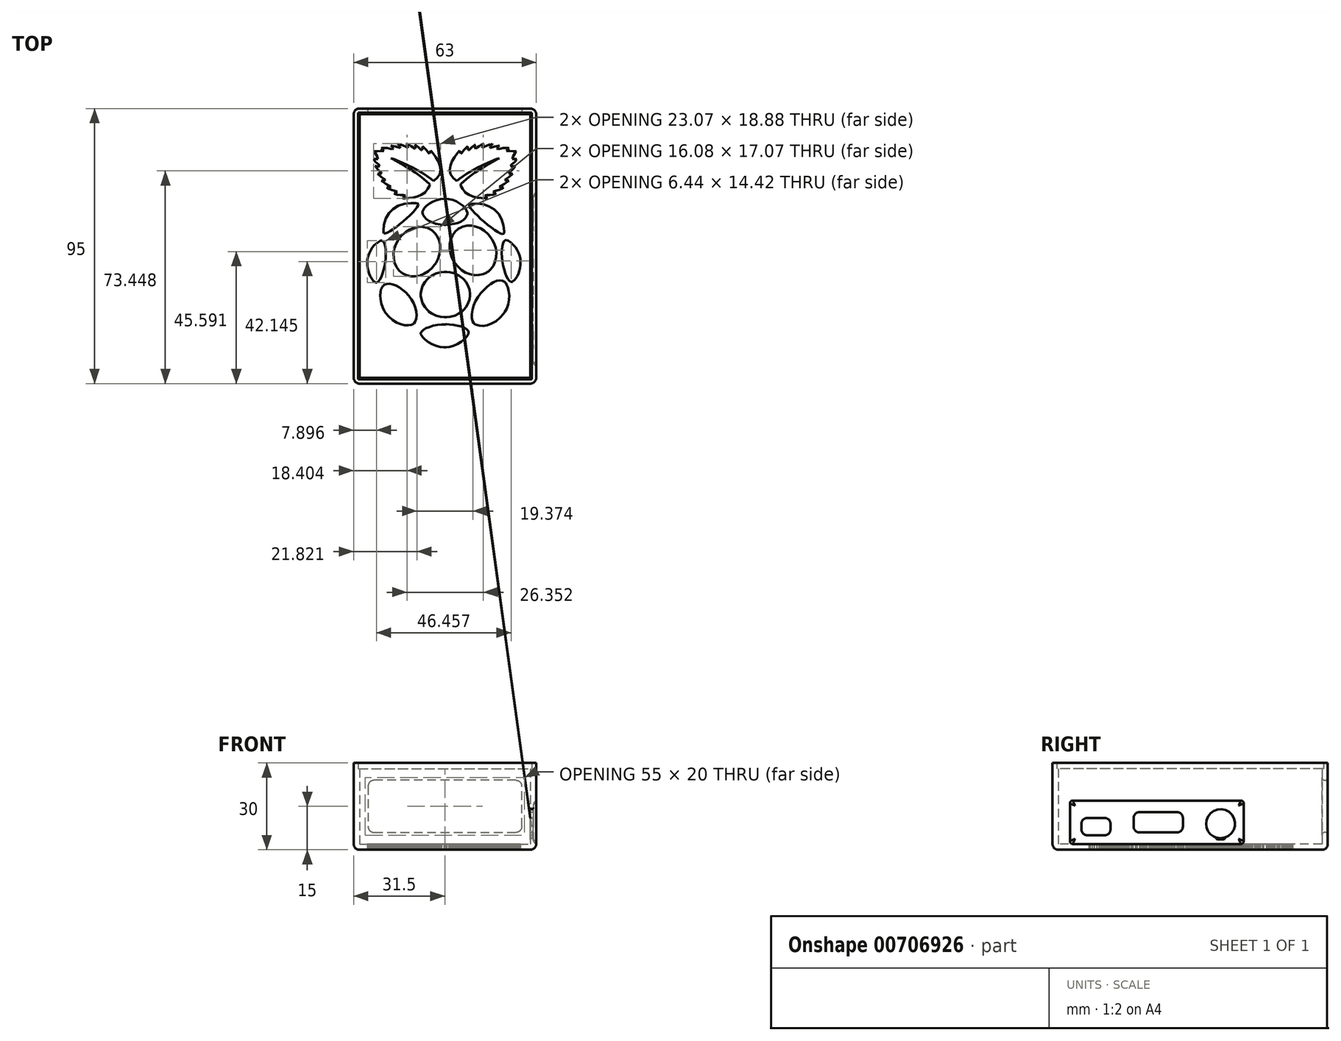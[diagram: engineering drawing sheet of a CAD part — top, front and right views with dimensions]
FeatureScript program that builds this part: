
annotation { "Feature Type Name" : "Feature", "Feature Type Description" : "" }
export const myFeature = defineFeature(function(context is Context, id is Id, definition is map)
    precondition{}
    {
        {
            var Q0;
            Q0=qCreatedBy(makeId("Top.planeOp"),FACE);
            var sketch = newSketch(context, id + "F0", { "sketchPlane" : qUnion([Q0])});
            skLineSegment(sketch, "E0.bottom", {"start": v(-30, 46) * mm, "end": v(30, 46) * mm});
            skLineSegment(sketch, "E0.top", {"start": v(-30, -46) * mm, "end": v(30, -46) * mm});
            skLineSegment(sketch, "E0.left", {"start": v(-30, 46) * mm, "end": v(-30, -46) * mm});
            skLineSegment(sketch, "E0.right", {"start": v(30, 46) * mm, "end": v(30, -46) * mm});
            skLineSegment(sketch, "E1.bottom", {"start": v(-29.5, 45.5) * mm, "end": v(29.5, 45.5) * mm});
            skLineSegment(sketch, "E1.top", {"start": v(-29.5, -45.5) * mm, "end": v(29.5, -45.5) * mm});
            skLineSegment(sketch, "E1.left", {"start": v(-29.5, 45.5) * mm, "end": v(-29.5, -45.5) * mm});
            skLineSegment(sketch, "E1.right", {"start": v(29.5, 45.5) * mm, "end": v(29.5, -45.5) * mm});
            skLineSegment(sketch, "E2.bottom", {"start": v(-31.5, 47.5) * mm, "end": v(31.5, 47.5) * mm});
            skLineSegment(sketch, "E2.top", {"start": v(-31.5, -47.5) * mm, "end": v(31.5, -47.5) * mm});
            skLineSegment(sketch, "E2.left", {"start": v(-31.5, 47.5) * mm, "end": v(-31.5, -47.5) * mm});
            skLineSegment(sketch, "E2.right", {"start": v(31.5, 47.5) * mm, "end": v(31.5, -47.5) * mm});
            skPoint(sketch, "E3", {"position": v(-30, 0) * mm});
            skPoint(sketch, "E4", {"position": v(0, 46) * mm});
            skLineSegment(sketch, "E5", {"start": v(-13.39, 37.27) * mm, "end": v(-13.48, 37.27) * mm});
            skLineSegment(sketch, "E6", {"start": v(-13.48, 37.27) * mm, "end": v(-13.98, 37.15) * mm});
            skLineSegment(sketch, "E7", {"start": v(-13.98, 37.15) * mm, "end": v(-14.52, 36.85) * mm});
            skLineSegment(sketch, "E8", {"start": v(-14.52, 36.85) * mm, "end": v(-14.63, 36.76) * mm});
            skLineSegment(sketch, "E9", {"start": v(-14.63, 36.76) * mm, "end": v(-14.83, 36.84) * mm});
            skLineSegment(sketch, "E10", {"start": v(-14.83, 36.84) * mm, "end": v(-15.47, 37.02) * mm});
            skLineSegment(sketch, "E11", {"start": v(-15.47, 37.02) * mm, "end": v(-16.29, 37.1) * mm});
            skLineSegment(sketch, "E12", {"start": v(-16.29, 37.1) * mm, "end": v(-17.08, 36.94) * mm});
            skLineSegment(sketch, "E13", {"start": v(-17.08, 36.94) * mm, "end": v(-17.67, 36.6) * mm});
            skLineSegment(sketch, "E14", {"start": v(-17.67, 36.6) * mm, "end": v(-17.83, 36.46) * mm});
            skLineSegment(sketch, "E15", {"start": v(-17.83, 36.46) * mm, "end": v(-18.07, 36.5) * mm});
            skLineSegment(sketch, "E16", {"start": v(-18.07, 36.5) * mm, "end": v(-18.79, 36.5) * mm});
            skLineSegment(sketch, "E17", {"start": v(-18.79, 36.5) * mm, "end": v(-19.44, 36.37) * mm});
            skLineSegment(sketch, "E18", {"start": v(-19.44, 36.37) * mm, "end": v(-19.89, 36.11) * mm});
            skLineSegment(sketch, "E19", {"start": v(-19.89, 36.11) * mm, "end": v(-20.13, 35.87) * mm});
            skLineSegment(sketch, "E20", {"start": v(-20.13, 35.87) * mm, "end": v(-20.2, 35.78) * mm});
            skLineSegment(sketch, "E21", {"start": v(-20.2, 35.78) * mm, "end": v(-20.25, 35.78) * mm});
            skLineSegment(sketch, "E22", {"start": v(-20.25, 35.78) * mm, "end": v(-20.4, 35.8) * mm});
            skLineSegment(sketch, "E23", {"start": v(-20.4, 35.8) * mm, "end": v(-20.75, 35.81) * mm});
            skLineSegment(sketch, "E24", {"start": v(-20.75, 35.81) * mm, "end": v(-21.19, 35.81) * mm});
            skLineSegment(sketch, "E25", {"start": v(-21.19, 35.81) * mm, "end": v(-21.7, 35.77) * mm});
            skLineSegment(sketch, "E26", {"start": v(-21.7, 35.77) * mm, "end": v(-22.23, 35.66) * mm});
            skLineSegment(sketch, "E27", {"start": v(-22.23, 35.66) * mm, "end": v(-22.76, 35.45) * mm});
            skLineSegment(sketch, "E28", {"start": v(-22.76, 35.45) * mm, "end": v(-23.25, 35.12) * mm});
            skLineSegment(sketch, "E29", {"start": v(-23.25, 35.12) * mm, "end": v(-23.58, 34.78) * mm});
            skLineSegment(sketch, "E30", {"start": v(-23.58, 34.78) * mm, "end": v(-23.67, 34.65) * mm});
            skLineSegment(sketch, "E31", {"start": v(-23.67, 34.65) * mm, "end": v(-23.88, 34.68) * mm});
            skLineSegment(sketch, "E32", {"start": v(-23.88, 34.68) * mm, "end": v(-24.52, 34.67) * mm});
            skLineSegment(sketch, "E33", {"start": v(-24.52, 34.67) * mm, "end": v(-25.21, 34.52) * mm});
            skLineSegment(sketch, "E34", {"start": v(-25.21, 34.52) * mm, "end": v(-25.74, 34.23) * mm});
            skLineSegment(sketch, "E35", {"start": v(-25.74, 34.23) * mm, "end": v(-26.12, 33.83) * mm});
            skLineSegment(sketch, "E36", {"start": v(-26.12, 33.83) * mm, "end": v(-26.34, 33.33) * mm});
            skLineSegment(sketch, "E37", {"start": v(-26.34, 33.33) * mm, "end": v(-26.4, 32.77) * mm});
            skLineSegment(sketch, "E38", {"start": v(-26.4, 32.77) * mm, "end": v(-26.3, 32.18) * mm});
            skLineSegment(sketch, "E39", {"start": v(-26.3, 32.18) * mm, "end": v(-26.12, 31.7) * mm});
            skLineSegment(sketch, "E40", {"start": v(-26.12, 31.7) * mm, "end": v(-26.04, 31.56) * mm});
            skLineSegment(sketch, "E41", {"start": v(-26.04, 31.56) * mm, "end": v(-26.14, 31.42) * mm});
            skLineSegment(sketch, "E42", {"start": v(-26.14, 31.42) * mm, "end": v(-26.4, 30.96) * mm});
            skLineSegment(sketch, "E43", {"start": v(-26.4, 30.96) * mm, "end": v(-26.6, 30.3) * mm});
            skLineSegment(sketch, "E44", {"start": v(-26.6, 30.3) * mm, "end": v(-26.48, 29.5) * mm});
            skLineSegment(sketch, "E45", {"start": v(-26.48, 29.5) * mm, "end": v(-26.07, 28.74) * mm});
            skLineSegment(sketch, "E46", {"start": v(-26.07, 28.74) * mm, "end": v(-25.9, 28.51) * mm});
            skLineSegment(sketch, "E47", {"start": v(-25.9, 28.51) * mm, "end": v(-25.96, 28.37) * mm});
            skLineSegment(sketch, "E48", {"start": v(-25.96, 28.37) * mm, "end": v(-26.08, 27.87) * mm});
            skLineSegment(sketch, "E49", {"start": v(-26.08, 27.87) * mm, "end": v(-26, 27.2) * mm});
            skLineSegment(sketch, "E50", {"start": v(-26, 27.2) * mm, "end": v(-25.67, 26.47) * mm});
            skLineSegment(sketch, "E51", {"start": v(-25.67, 26.47) * mm, "end": v(-25.23, 25.87) * mm});
            skLineSegment(sketch, "E52", {"start": v(-25.23, 25.87) * mm, "end": v(-25.06, 25.69) * mm});
            skLineSegment(sketch, "E53", {"start": v(-25.06, 25.69) * mm, "end": v(-25.1, 25.49) * mm});
            skLineSegment(sketch, "E54", {"start": v(-25.1, 25.49) * mm, "end": v(-25.12, 24.87) * mm});
            skLineSegment(sketch, "E55", {"start": v(-25.12, 24.87) * mm, "end": v(-24.92, 24.17) * mm});
            skLineSegment(sketch, "E56", {"start": v(-24.92, 24.17) * mm, "end": v(-24.5, 23.57) * mm});
            skLineSegment(sketch, "E57", {"start": v(-24.5, 23.57) * mm, "end": v(-24.06, 23.16) * mm});
            skLineSegment(sketch, "E58", {"start": v(-24.06, 23.16) * mm, "end": v(-23.9, 23.05) * mm});
            skLineSegment(sketch, "E59", {"start": v(-23.9, 23.05) * mm, "end": v(-23.92, 22.79) * mm});
            skLineSegment(sketch, "E60", {"start": v(-23.92, 22.79) * mm, "end": v(-23.73, 21.97) * mm});
            skLineSegment(sketch, "E61", {"start": v(-23.73, 21.97) * mm, "end": v(-23.16, 21.14) * mm});
            skLineSegment(sketch, "E62", {"start": v(-23.16, 21.14) * mm, "end": v(-22.47, 20.55) * mm});
            skLineSegment(sketch, "E63", {"start": v(-22.47, 20.55) * mm, "end": v(-22.06, 20.27) * mm});
            skLineSegment(sketch, "E64", {"start": v(-22.06, 20.27) * mm, "end": v(-21.94, 20.19) * mm});
            skLineSegment(sketch, "E65", {"start": v(-21.94, 20.19) * mm, "end": v(-21.9, 20.01) * mm});
            skLineSegment(sketch, "E66", {"start": v(-21.9, 20.01) * mm, "end": v(-21.74, 19.5) * mm});
            skLineSegment(sketch, "E67", {"start": v(-21.74, 19.5) * mm, "end": v(-21.34, 18.87) * mm});
            skLineSegment(sketch, "E68", {"start": v(-21.34, 18.87) * mm, "end": v(-20.63, 18.32) * mm});
            skLineSegment(sketch, "E69", {"start": v(-20.63, 18.32) * mm, "end": v(-19.78, 17.97) * mm});
            skLineSegment(sketch, "E70", {"start": v(-19.78, 17.97) * mm, "end": v(-19.49, 17.89) * mm});
            skLineSegment(sketch, "E71", {"start": v(-19.49, 17.89) * mm, "end": v(-19.44, 17.67) * mm});
            skLineSegment(sketch, "E72", {"start": v(-19.44, 17.67) * mm, "end": v(-19.12, 17.04) * mm});
            skLineSegment(sketch, "E73", {"start": v(-19.12, 17.04) * mm, "end": v(-18.52, 16.52) * mm});
            skLineSegment(sketch, "E74", {"start": v(-18.52, 16.52) * mm, "end": v(-17.78, 16.2) * mm});
            skLineSegment(sketch, "E75", {"start": v(-17.78, 16.2) * mm, "end": v(-17.17, 16.02) * mm});
            skLineSegment(sketch, "E76", {"start": v(-17.17, 16.02) * mm, "end": v(-16.96, 15.97) * mm});
            skLineSegment(sketch, "E77", {"start": v(-16.96, 15.97) * mm, "end": v(-17.3, 15.77) * mm});
            skLineSegment(sketch, "E78", {"start": v(-17.3, 15.77) * mm, "end": v(-18.29, 15.15) * mm});
            skLineSegment(sketch, "E79", {"start": v(-18.29, 15.15) * mm, "end": v(-19.53, 14.22) * mm});
            skLineSegment(sketch, "E80", {"start": v(-19.53, 14.22) * mm, "end": v(-20.66, 13.16) * mm});
            skLineSegment(sketch, "E81", {"start": v(-20.66, 13.16) * mm, "end": v(-21.66, 11.92) * mm});
            skLineSegment(sketch, "E82", {"start": v(-21.66, 11.92) * mm, "end": v(-22.48, 10.46) * mm});
            skLineSegment(sketch, "E83", {"start": v(-22.48, 10.46) * mm, "end": v(-23.1, 8.74) * mm});
            skLineSegment(sketch, "E84", {"start": v(-23.1, 8.74) * mm, "end": v(-23.5, 6.72) * mm});
            skLineSegment(sketch, "E85", {"start": v(-23.5, 6.72) * mm, "end": v(-23.63, 4.96) * mm});
            skLineSegment(sketch, "E86", {"start": v(-23.63, 4.96) * mm, "end": v(-23.63, 4.37) * mm});
            skLineSegment(sketch, "E87", {"start": v(-23.63, 4.37) * mm, "end": v(-24.16, 3.43) * mm});
            skLineSegment(sketch, "E88", {"start": v(-24.16, 3.43) * mm, "end": v(-24.36, 3.3) * mm});
            skLineSegment(sketch, "E89", {"start": v(-24.36, 3.3) * mm, "end": v(-24.93, 2.9) * mm});
            skLineSegment(sketch, "E90", {"start": v(-24.93, 2.9) * mm, "end": v(-25.67, 2.24) * mm});
            skLineSegment(sketch, "E91", {"start": v(-25.67, 2.24) * mm, "end": v(-26.38, 1.47) * mm});
            skLineSegment(sketch, "E92", {"start": v(-26.38, 1.47) * mm, "end": v(-27.04, 0.61) * mm});
            skLineSegment(sketch, "E93", {"start": v(-27.04, 0.61) * mm, "end": v(-27.63, -0.34) * mm});
            skLineSegment(sketch, "E94", {"start": v(-27.63, -0.34) * mm, "end": v(-28.15, -1.37) * mm});
            skLineSegment(sketch, "E95", {"start": v(-28.15, -1.37) * mm, "end": v(-28.58, -2.47) * mm});
            skLineSegment(sketch, "E96", {"start": v(-28.58, -2.47) * mm, "end": v(-28.9, -3.62) * mm});
            skLineSegment(sketch, "E97", {"start": v(-28.9, -3.62) * mm, "end": v(-29.11, -4.83) * mm});
            skLineSegment(sketch, "E98", {"start": v(-29.11, -4.83) * mm, "end": v(-29.2, -6.07) * mm});
            skLineSegment(sketch, "E99", {"start": v(-29.2, -6.07) * mm, "end": v(-29.13, -7.34) * mm});
            skLineSegment(sketch, "E100", {"start": v(-29.13, -7.34) * mm, "end": v(-28.9, -8.62) * mm});
            skLineSegment(sketch, "E101", {"start": v(-28.9, -8.62) * mm, "end": v(-28.52, -9.9) * mm});
            skLineSegment(sketch, "E102", {"start": v(-28.52, -9.9) * mm, "end": v(-27.94, -11.2) * mm});
            skLineSegment(sketch, "E103", {"start": v(-27.94, -11.2) * mm, "end": v(-27.17, -12.47) * mm});
            skLineSegment(sketch, "E104", {"start": v(-27.17, -12.47) * mm, "end": v(-26.46, -13.42) * mm});
            skLineSegment(sketch, "E105", {"start": v(-26.46, -13.42) * mm, "end": v(-26.2, -13.71) * mm});
            skLineSegment(sketch, "E106", {"start": v(-26.2, -13.71) * mm, "end": v(-26.13, -14.07) * mm});
            skLineSegment(sketch, "E107", {"start": v(-26.13, -14.07) * mm, "end": v(-25.87, -15.15) * mm});
            skLineSegment(sketch, "E108", {"start": v(-25.87, -15.15) * mm, "end": v(-25.47, -16.45) * mm});
            skLineSegment(sketch, "E109", {"start": v(-25.47, -16.45) * mm, "end": v(-25.04, -17.66) * mm});
            skLineSegment(sketch, "E110", {"start": v(-25.04, -17.66) * mm, "end": v(-24.72, -18.57) * mm});
            skLineSegment(sketch, "E111", {"start": v(-24.72, -18.57) * mm, "end": v(-24.61, -18.87) * mm});
            skLineSegment(sketch, "E112", {"start": v(-24.61, -18.87) * mm, "end": v(-24.54, -19.45) * mm});
            skLineSegment(sketch, "E113", {"start": v(-24.54, -19.45) * mm, "end": v(-24.1, -21.17) * mm});
            skLineSegment(sketch, "E114", {"start": v(-24.1, -21.17) * mm, "end": v(-23.23, -23.16) * mm});
            skLineSegment(sketch, "E115", {"start": v(-23.23, -23.16) * mm, "end": v(-22.14, -24.84) * mm});
            skLineSegment(sketch, "E116", {"start": v(-22.14, -24.84) * mm, "end": v(-20.92, -26.2) * mm});
            skLineSegment(sketch, "E117", {"start": v(-20.92, -26.2) * mm, "end": v(-19.67, -27.3) * mm});
            skLineSegment(sketch, "E118", {"start": v(-19.67, -27.3) * mm, "end": v(-18.5, -28.1) * mm});
            skLineSegment(sketch, "E119", {"start": v(-18.5, -28.1) * mm, "end": v(-17.5, -28.62) * mm});
            skLineSegment(sketch, "E120", {"start": v(-17.5, -28.62) * mm, "end": v(-16.96, -28.84) * mm});
            skLineSegment(sketch, "E121", {"start": v(-16.96, -28.84) * mm, "end": v(-16.78, -28.9) * mm});
            skLineSegment(sketch, "E122", {"start": v(-16.78, -28.9) * mm, "end": v(-16.37, -29.2) * mm});
            skLineSegment(sketch, "E123", {"start": v(-16.37, -29.2) * mm, "end": v(-15.14, -30.09) * mm});
            skLineSegment(sketch, "E124", {"start": v(-15.14, -30.09) * mm, "end": v(-13.38, -31.22) * mm});
            skLineSegment(sketch, "E125", {"start": v(-13.38, -31.22) * mm, "end": v(-11.45, -32.25) * mm});
            skLineSegment(sketch, "E126", {"start": v(-11.45, -32.25) * mm, "end": v(-9.83, -32.95) * mm});
            skLineSegment(sketch, "E127", {"start": v(-9.83, -32.95) * mm, "end": v(-9.28, -33.15) * mm});
            skLineSegment(sketch, "E128", {"start": v(-9.28, -33.15) * mm, "end": v(-8.77, -33.67) * mm});
            skLineSegment(sketch, "E129", {"start": v(-8.77, -33.67) * mm, "end": v(-7.06, -35.05) * mm});
            skLineSegment(sketch, "E130", {"start": v(-7.06, -35.05) * mm, "end": v(-4.77, -36.34) * mm});
            skLineSegment(sketch, "E131", {"start": v(-4.77, -36.34) * mm, "end": v(-2.44, -37.05) * mm});
            skLineSegment(sketch, "E132", {"start": v(-2.44, -37.05) * mm, "end": v(-0.66, -37.28) * mm});
            skLineSegment(sketch, "E133", {"start": v(-0.66, -37.28) * mm, "end": v(-0.07, -37.28) * mm});
            skLineSegment(sketch, "E134", {"start": v(-0.07, -37.28) * mm, "end": v(-0.04, -37.28) * mm});
            skLineSegment(sketch, "E135", {"start": v(-0.04, -37.28) * mm, "end": v(0.06, -37.28) * mm});
            skLineSegment(sketch, "E136", {"start": v(0.06, -37.28) * mm, "end": v(0.07, -37.28) * mm});
            skLineSegment(sketch, "E137", {"start": v(0.07, -37.28) * mm, "end": v(0.66, -37.28) * mm});
            skLineSegment(sketch, "E138", {"start": v(0.66, -37.28) * mm, "end": v(2.44, -37.06) * mm});
            skLineSegment(sketch, "E139", {"start": v(2.44, -37.06) * mm, "end": v(4.77, -36.34) * mm});
            skLineSegment(sketch, "E140", {"start": v(4.77, -36.34) * mm, "end": v(7.06, -35.05) * mm});
            skLineSegment(sketch, "E141", {"start": v(7.06, -35.05) * mm, "end": v(8.77, -33.67) * mm});
            skLineSegment(sketch, "E142", {"start": v(8.77, -33.67) * mm, "end": v(9.28, -33.15) * mm});
            skLineSegment(sketch, "E143", {"start": v(9.28, -33.15) * mm, "end": v(9.83, -32.95) * mm});
            skLineSegment(sketch, "E144", {"start": v(9.83, -32.95) * mm, "end": v(11.45, -32.25) * mm});
            skLineSegment(sketch, "E145", {"start": v(11.45, -32.25) * mm, "end": v(13.38, -31.22) * mm});
            skLineSegment(sketch, "E146", {"start": v(13.38, -31.22) * mm, "end": v(15.14, -30.09) * mm});
            skLineSegment(sketch, "E147", {"start": v(15.14, -30.09) * mm, "end": v(16.37, -29.2) * mm});
            skLineSegment(sketch, "E148", {"start": v(16.37, -29.2) * mm, "end": v(16.78, -28.9) * mm});
            skLineSegment(sketch, "E149", {"start": v(16.78, -28.9) * mm, "end": v(16.96, -28.84) * mm});
            skLineSegment(sketch, "E150", {"start": v(16.96, -28.84) * mm, "end": v(17.5, -28.62) * mm});
            skLineSegment(sketch, "E151", {"start": v(17.5, -28.62) * mm, "end": v(18.5, -28.1) * mm});
            skLineSegment(sketch, "E152", {"start": v(18.5, -28.1) * mm, "end": v(19.67, -27.3) * mm});
            skLineSegment(sketch, "E153", {"start": v(19.67, -27.3) * mm, "end": v(20.92, -26.2) * mm});
            skLineSegment(sketch, "E154", {"start": v(20.92, -26.2) * mm, "end": v(22.14, -24.84) * mm});
            skLineSegment(sketch, "E155", {"start": v(22.14, -24.84) * mm, "end": v(23.23, -23.16) * mm});
            skLineSegment(sketch, "E156", {"start": v(23.23, -23.16) * mm, "end": v(24.1, -21.17) * mm});
            skLineSegment(sketch, "E157", {"start": v(24.1, -21.17) * mm, "end": v(24.54, -19.45) * mm});
            skLineSegment(sketch, "E158", {"start": v(24.54, -19.45) * mm, "end": v(24.61, -18.87) * mm});
            skLineSegment(sketch, "E159", {"start": v(24.61, -18.87) * mm, "end": v(24.72, -18.57) * mm});
            skLineSegment(sketch, "E160", {"start": v(24.72, -18.57) * mm, "end": v(25.04, -17.66) * mm});
            skLineSegment(sketch, "E161", {"start": v(25.04, -17.66) * mm, "end": v(25.47, -16.45) * mm});
            skLineSegment(sketch, "E162", {"start": v(25.47, -16.45) * mm, "end": v(25.87, -15.15) * mm});
            skLineSegment(sketch, "E163", {"start": v(25.87, -15.15) * mm, "end": v(26.13, -14.07) * mm});
            skLineSegment(sketch, "E164", {"start": v(26.13, -14.07) * mm, "end": v(26.2, -13.71) * mm});
            skLineSegment(sketch, "E165", {"start": v(26.2, -13.71) * mm, "end": v(26.46, -13.42) * mm});
            skLineSegment(sketch, "E166", {"start": v(26.46, -13.42) * mm, "end": v(27.17, -12.47) * mm});
            skLineSegment(sketch, "E167", {"start": v(27.17, -12.47) * mm, "end": v(27.94, -11.2) * mm});
            skLineSegment(sketch, "E168", {"start": v(27.94, -11.2) * mm, "end": v(28.52, -9.9) * mm});
            skLineSegment(sketch, "E169", {"start": v(28.52, -9.9) * mm, "end": v(28.9, -8.62) * mm});
            skLineSegment(sketch, "E170", {"start": v(28.9, -8.62) * mm, "end": v(29.13, -7.34) * mm});
            skLineSegment(sketch, "E171", {"start": v(29.13, -7.34) * mm, "end": v(29.2, -6.07) * mm});
            skLineSegment(sketch, "E172", {"start": v(29.2, -6.07) * mm, "end": v(29.11, -4.83) * mm});
            skLineSegment(sketch, "E173", {"start": v(29.11, -4.83) * mm, "end": v(28.9, -3.62) * mm});
            skLineSegment(sketch, "E174", {"start": v(28.9, -3.62) * mm, "end": v(28.58, -2.47) * mm});
            skLineSegment(sketch, "E175", {"start": v(28.58, -2.47) * mm, "end": v(28.15, -1.37) * mm});
            skLineSegment(sketch, "E176", {"start": v(28.15, -1.37) * mm, "end": v(27.63, -0.34) * mm});
            skLineSegment(sketch, "E177", {"start": v(27.63, -0.34) * mm, "end": v(27.03, 0.61) * mm});
            skLineSegment(sketch, "E178", {"start": v(27.03, 0.61) * mm, "end": v(26.38, 1.48) * mm});
            skLineSegment(sketch, "E179", {"start": v(26.38, 1.48) * mm, "end": v(25.67, 2.24) * mm});
            skLineSegment(sketch, "E180", {"start": v(25.67, 2.24) * mm, "end": v(24.93, 2.9) * mm});
            skLineSegment(sketch, "E181", {"start": v(24.93, 2.9) * mm, "end": v(24.36, 3.3) * mm});
            skLineSegment(sketch, "E182", {"start": v(24.36, 3.3) * mm, "end": v(24.16, 3.43) * mm});
            skLineSegment(sketch, "E183", {"start": v(24.16, 3.43) * mm, "end": v(23.63, 4.37) * mm});
            skLineSegment(sketch, "E184", {"start": v(23.63, 4.37) * mm, "end": v(23.63, 4.96) * mm});
            skLineSegment(sketch, "E185", {"start": v(23.63, 4.96) * mm, "end": v(23.5, 6.72) * mm});
            skLineSegment(sketch, "E186", {"start": v(23.5, 6.72) * mm, "end": v(23.1, 8.74) * mm});
            skLineSegment(sketch, "E187", {"start": v(23.1, 8.74) * mm, "end": v(22.48, 10.46) * mm});
            skLineSegment(sketch, "E188", {"start": v(22.48, 10.46) * mm, "end": v(21.65, 11.92) * mm});
            skLineSegment(sketch, "E189", {"start": v(21.65, 11.92) * mm, "end": v(20.66, 13.16) * mm});
            skLineSegment(sketch, "E190", {"start": v(20.66, 13.16) * mm, "end": v(19.53, 14.22) * mm});
            skLineSegment(sketch, "E191", {"start": v(19.53, 14.22) * mm, "end": v(18.28, 15.15) * mm});
            skLineSegment(sketch, "E192", {"start": v(18.28, 15.15) * mm, "end": v(17.3, 15.77) * mm});
            skLineSegment(sketch, "E193", {"start": v(17.3, 15.77) * mm, "end": v(16.96, 15.97) * mm});
            skLineSegment(sketch, "E194", {"start": v(16.96, 15.97) * mm, "end": v(17.17, 16.02) * mm});
            skLineSegment(sketch, "E195", {"start": v(17.17, 16.02) * mm, "end": v(17.77, 16.2) * mm});
            skLineSegment(sketch, "E196", {"start": v(17.77, 16.2) * mm, "end": v(18.52, 16.52) * mm});
            skLineSegment(sketch, "E197", {"start": v(18.52, 16.52) * mm, "end": v(19.12, 17.05) * mm});
            skLineSegment(sketch, "E198", {"start": v(19.12, 17.05) * mm, "end": v(19.44, 17.67) * mm});
            skLineSegment(sketch, "E199", {"start": v(19.44, 17.67) * mm, "end": v(19.49, 17.9) * mm});
            skLineSegment(sketch, "E200", {"start": v(19.49, 17.9) * mm, "end": v(19.78, 17.97) * mm});
            skLineSegment(sketch, "E201", {"start": v(19.78, 17.97) * mm, "end": v(20.63, 18.32) * mm});
            skLineSegment(sketch, "E202", {"start": v(20.63, 18.32) * mm, "end": v(21.34, 18.87) * mm});
            skLineSegment(sketch, "E203", {"start": v(21.34, 18.87) * mm, "end": v(21.74, 19.5) * mm});
            skLineSegment(sketch, "E204", {"start": v(21.74, 19.5) * mm, "end": v(21.9, 20.02) * mm});
            skLineSegment(sketch, "E205", {"start": v(21.9, 20.02) * mm, "end": v(21.94, 20.19) * mm});
            skLineSegment(sketch, "E206", {"start": v(21.94, 20.19) * mm, "end": v(22.06, 20.27) * mm});
            skLineSegment(sketch, "E207", {"start": v(22.06, 20.27) * mm, "end": v(22.47, 20.55) * mm});
            skLineSegment(sketch, "E208", {"start": v(22.47, 20.55) * mm, "end": v(23.16, 21.14) * mm});
            skLineSegment(sketch, "E209", {"start": v(23.16, 21.14) * mm, "end": v(23.73, 21.97) * mm});
            skLineSegment(sketch, "E210", {"start": v(23.73, 21.97) * mm, "end": v(23.92, 22.79) * mm});
            skLineSegment(sketch, "E211", {"start": v(23.92, 22.79) * mm, "end": v(23.9, 23.05) * mm});
            skLineSegment(sketch, "E212", {"start": v(23.9, 23.05) * mm, "end": v(24.06, 23.16) * mm});
            skLineSegment(sketch, "E213", {"start": v(24.06, 23.16) * mm, "end": v(24.5, 23.57) * mm});
            skLineSegment(sketch, "E214", {"start": v(24.5, 23.57) * mm, "end": v(24.92, 24.17) * mm});
            skLineSegment(sketch, "E215", {"start": v(24.92, 24.17) * mm, "end": v(25.12, 24.87) * mm});
            skLineSegment(sketch, "E216", {"start": v(25.12, 24.87) * mm, "end": v(25.1, 25.5) * mm});
            skLineSegment(sketch, "E217", {"start": v(25.1, 25.5) * mm, "end": v(25.06, 25.69) * mm});
            skLineSegment(sketch, "E218", {"start": v(25.06, 25.69) * mm, "end": v(25.23, 25.87) * mm});
            skLineSegment(sketch, "E219", {"start": v(25.23, 25.87) * mm, "end": v(25.67, 26.47) * mm});
            skLineSegment(sketch, "E220", {"start": v(25.67, 26.47) * mm, "end": v(26, 27.2) * mm});
            skLineSegment(sketch, "E221", {"start": v(26, 27.2) * mm, "end": v(26.08, 27.87) * mm});
            skLineSegment(sketch, "E222", {"start": v(26.08, 27.87) * mm, "end": v(25.96, 28.37) * mm});
            skLineSegment(sketch, "E223", {"start": v(25.96, 28.37) * mm, "end": v(25.89, 28.51) * mm});
            skLineSegment(sketch, "E224", {"start": v(25.89, 28.51) * mm, "end": v(26.07, 28.74) * mm});
            skLineSegment(sketch, "E225", {"start": v(26.07, 28.74) * mm, "end": v(26.48, 29.5) * mm});
            skLineSegment(sketch, "E226", {"start": v(26.48, 29.5) * mm, "end": v(26.6, 30.3) * mm});
            skLineSegment(sketch, "E227", {"start": v(26.6, 30.3) * mm, "end": v(26.4, 30.97) * mm});
            skLineSegment(sketch, "E228", {"start": v(26.4, 30.97) * mm, "end": v(26.14, 31.42) * mm});
            skLineSegment(sketch, "E229", {"start": v(26.14, 31.42) * mm, "end": v(26.04, 31.56) * mm});
            skLineSegment(sketch, "E230", {"start": v(26.04, 31.56) * mm, "end": v(26.12, 31.7) * mm});
            skLineSegment(sketch, "E231", {"start": v(26.12, 31.7) * mm, "end": v(26.3, 32.18) * mm});
            skLineSegment(sketch, "E232", {"start": v(26.3, 32.18) * mm, "end": v(26.4, 32.77) * mm});
            skLineSegment(sketch, "E233", {"start": v(26.4, 32.77) * mm, "end": v(26.33, 33.33) * mm});
            skLineSegment(sketch, "E234", {"start": v(26.33, 33.33) * mm, "end": v(26.12, 33.83) * mm});
            skLineSegment(sketch, "E235", {"start": v(26.12, 33.83) * mm, "end": v(25.74, 34.23) * mm});
            skLineSegment(sketch, "E236", {"start": v(25.74, 34.23) * mm, "end": v(25.2, 34.52) * mm});
            skLineSegment(sketch, "E237", {"start": v(25.2, 34.52) * mm, "end": v(24.52, 34.67) * mm});
            skLineSegment(sketch, "E238", {"start": v(24.52, 34.67) * mm, "end": v(23.88, 34.68) * mm});
            skLineSegment(sketch, "E239", {"start": v(23.88, 34.68) * mm, "end": v(23.67, 34.65) * mm});
            skLineSegment(sketch, "E240", {"start": v(23.67, 34.65) * mm, "end": v(23.58, 34.78) * mm});
            skLineSegment(sketch, "E241", {"start": v(23.58, 34.78) * mm, "end": v(23.25, 35.12) * mm});
            skLineSegment(sketch, "E242", {"start": v(23.25, 35.12) * mm, "end": v(22.76, 35.45) * mm});
            skLineSegment(sketch, "E243", {"start": v(22.76, 35.45) * mm, "end": v(22.23, 35.66) * mm});
            skLineSegment(sketch, "E244", {"start": v(22.23, 35.66) * mm, "end": v(21.7, 35.77) * mm});
            skLineSegment(sketch, "E245", {"start": v(21.7, 35.77) * mm, "end": v(21.19, 35.81) * mm});
            skLineSegment(sketch, "E246", {"start": v(21.19, 35.81) * mm, "end": v(20.75, 35.81) * mm});
            skLineSegment(sketch, "E247", {"start": v(20.75, 35.81) * mm, "end": v(20.4, 35.8) * mm});
            skLineSegment(sketch, "E248", {"start": v(20.4, 35.8) * mm, "end": v(20.25, 35.78) * mm});
            skLineSegment(sketch, "E249", {"start": v(20.25, 35.78) * mm, "end": v(20.2, 35.78) * mm});
            skLineSegment(sketch, "E250", {"start": v(20.2, 35.78) * mm, "end": v(20.13, 35.87) * mm});
            skLineSegment(sketch, "E251", {"start": v(20.13, 35.87) * mm, "end": v(19.89, 36.11) * mm});
            skLineSegment(sketch, "E252", {"start": v(19.89, 36.11) * mm, "end": v(19.44, 36.37) * mm});
            skLineSegment(sketch, "E253", {"start": v(19.44, 36.37) * mm, "end": v(18.78, 36.5) * mm});
            skLineSegment(sketch, "E254", {"start": v(18.78, 36.5) * mm, "end": v(18.07, 36.5) * mm});
            skLineSegment(sketch, "E255", {"start": v(18.07, 36.5) * mm, "end": v(17.83, 36.46) * mm});
            skLineSegment(sketch, "E256", {"start": v(17.83, 36.46) * mm, "end": v(17.67, 36.6) * mm});
            skLineSegment(sketch, "E257", {"start": v(17.67, 36.6) * mm, "end": v(17.08, 36.94) * mm});
            skLineSegment(sketch, "E258", {"start": v(17.08, 36.94) * mm, "end": v(16.29, 37.1) * mm});
            skLineSegment(sketch, "E259", {"start": v(16.29, 37.1) * mm, "end": v(15.47, 37.02) * mm});
            skLineSegment(sketch, "E260", {"start": v(15.47, 37.02) * mm, "end": v(14.83, 36.84) * mm});
            skLineSegment(sketch, "E261", {"start": v(14.83, 36.84) * mm, "end": v(14.63, 36.76) * mm});
            skLineSegment(sketch, "E262", {"start": v(14.63, 36.76) * mm, "end": v(14.43, 36.92) * mm});
            skLineSegment(sketch, "E263", {"start": v(14.43, 36.92) * mm, "end": v(13.7, 37.23) * mm});
            skLineSegment(sketch, "E264", {"start": v(13.7, 37.23) * mm, "end": v(12.89, 37.22) * mm});
            skLineSegment(sketch, "E265", {"start": v(12.89, 37.22) * mm, "end": v(12.14, 36.95) * mm});
            skLineSegment(sketch, "E266", {"start": v(12.14, 36.95) * mm, "end": v(11.58, 36.71) * mm});
            skLineSegment(sketch, "E267", {"start": v(11.58, 36.71) * mm, "end": v(11.4, 36.65) * mm});
            skLineSegment(sketch, "E268", {"start": v(11.4, 36.65) * mm, "end": v(11.15, 36.73) * mm});
            skLineSegment(sketch, "E269", {"start": v(11.15, 36.73) * mm, "end": v(10.38, 36.84) * mm});
            skLineSegment(sketch, "E270", {"start": v(10.38, 36.84) * mm, "end": v(9.69, 36.71) * mm});
            skLineSegment(sketch, "E271", {"start": v(9.69, 36.71) * mm, "end": v(9.15, 36.43) * mm});
            skLineSegment(sketch, "E272", {"start": v(9.15, 36.43) * mm, "end": v(8.74, 36.21) * mm});
            skLineSegment(sketch, "E273", {"start": v(8.74, 36.21) * mm, "end": v(8.6, 36.16) * mm});
            skLineSegment(sketch, "E274", {"start": v(8.6, 36.16) * mm, "end": v(8.33, 36.22) * mm});
            skLineSegment(sketch, "E275", {"start": v(8.33, 36.22) * mm, "end": v(7.48, 36.23) * mm});
            skLineSegment(sketch, "E276", {"start": v(7.48, 36.23) * mm, "end": v(6.68, 35.97) * mm});
            skLineSegment(sketch, "E277", {"start": v(6.68, 35.97) * mm, "end": v(6.05, 35.48) * mm});
            skLineSegment(sketch, "E278", {"start": v(6.05, 35.48) * mm, "end": v(5.6, 35.01) * mm});
            skLineSegment(sketch, "E279", {"start": v(5.6, 35.01) * mm, "end": v(5.45, 34.86) * mm});
            skLineSegment(sketch, "E280", {"start": v(5.45, 34.86) * mm, "end": v(4.46, 34.88) * mm});
            skLineSegment(sketch, "E281", {"start": v(4.46, 34.88) * mm, "end": v(4.21, 34.73) * mm});
            skLineSegment(sketch, "E282", {"start": v(4.21, 34.73) * mm, "end": v(3.52, 34.22) * mm});
            skLineSegment(sketch, "E283", {"start": v(3.52, 34.22) * mm, "end": v(2.7, 33.44) * mm});
            skLineSegment(sketch, "E284", {"start": v(2.7, 33.44) * mm, "end": v(2, 32.6) * mm});
            skLineSegment(sketch, "E285", {"start": v(2, 32.6) * mm, "end": v(1.4, 31.7) * mm});
            skLineSegment(sketch, "E286", {"start": v(1.4, 31.7) * mm, "end": v(0.91, 30.8) * mm});
            skLineSegment(sketch, "E287", {"start": v(0.91, 30.8) * mm, "end": v(0.52, 29.94) * mm});
            skLineSegment(sketch, "E288", {"start": v(0.52, 29.94) * mm, "end": v(0.22, 29.14) * mm});
            skLineSegment(sketch, "E289", {"start": v(0.22, 29.14) * mm, "end": v(0.05, 28.63) * mm});
            skLineSegment(sketch, "E290", {"start": v(0.05, 28.63) * mm, "end": v(0, 28.46) * mm});
            skLineSegment(sketch, "E291", {"start": v(0, 28.46) * mm, "end": v(-0.05, 28.63) * mm});
            skLineSegment(sketch, "E292", {"start": v(-0.05, 28.63) * mm, "end": v(-0.22, 29.14) * mm});
            skLineSegment(sketch, "E293", {"start": v(-0.22, 29.14) * mm, "end": v(-0.52, 29.94) * mm});
            skLineSegment(sketch, "E294", {"start": v(-0.52, 29.94) * mm, "end": v(-0.92, 30.8) * mm});
            skLineSegment(sketch, "E295", {"start": v(-0.92, 30.8) * mm, "end": v(-1.4, 31.7) * mm});
            skLineSegment(sketch, "E296", {"start": v(-1.4, 31.7) * mm, "end": v(-2, 32.6) * mm});
            skLineSegment(sketch, "E297", {"start": v(-2, 32.6) * mm, "end": v(-2.7, 33.44) * mm});
            skLineSegment(sketch, "E298", {"start": v(-2.7, 33.44) * mm, "end": v(-3.52, 34.22) * mm});
            skLineSegment(sketch, "E299", {"start": v(-3.52, 34.22) * mm, "end": v(-4.22, 34.73) * mm});
            skLineSegment(sketch, "E300", {"start": v(-4.22, 34.73) * mm, "end": v(-4.46, 34.88) * mm});
            skLineSegment(sketch, "E301", {"start": v(-4.46, 34.88) * mm, "end": v(-5.45, 34.86) * mm});
            skLineSegment(sketch, "E302", {"start": v(-5.45, 34.86) * mm, "end": v(-5.6, 35.01) * mm});
            skLineSegment(sketch, "E303", {"start": v(-5.6, 35.01) * mm, "end": v(-6.05, 35.48) * mm});
            skLineSegment(sketch, "E304", {"start": v(-6.05, 35.48) * mm, "end": v(-6.68, 35.97) * mm});
            skLineSegment(sketch, "E305", {"start": v(-6.68, 35.97) * mm, "end": v(-7.48, 36.23) * mm});
            skLineSegment(sketch, "E306", {"start": v(-7.48, 36.23) * mm, "end": v(-8.33, 36.22) * mm});
            skLineSegment(sketch, "E307", {"start": v(-8.33, 36.22) * mm, "end": v(-8.6, 36.16) * mm});
            skLineSegment(sketch, "E308", {"start": v(-8.6, 36.16) * mm, "end": v(-8.75, 36.21) * mm});
            skLineSegment(sketch, "E309", {"start": v(-8.75, 36.21) * mm, "end": v(-9.15, 36.43) * mm});
            skLineSegment(sketch, "E310", {"start": v(-9.15, 36.43) * mm, "end": v(-9.69, 36.71) * mm});
            skLineSegment(sketch, "E311", {"start": v(-9.69, 36.71) * mm, "end": v(-10.38, 36.84) * mm});
            skLineSegment(sketch, "E312", {"start": v(-10.38, 36.84) * mm, "end": v(-11.15, 36.73) * mm});
            skLineSegment(sketch, "E313", {"start": v(-11.15, 36.73) * mm, "end": v(-11.4, 36.65) * mm});
            skLineSegment(sketch, "E314", {"start": v(-11.4, 36.65) * mm, "end": v(-11.52, 36.69) * mm});
            skLineSegment(sketch, "E315", {"start": v(-11.52, 36.69) * mm, "end": v(-11.88, 36.84) * mm});
            skLineSegment(sketch, "E316", {"start": v(-11.88, 36.84) * mm, "end": v(-12.37, 37.05) * mm});
            skLineSegment(sketch, "E317", {"start": v(-12.37, 37.05) * mm, "end": v(-12.87, 37.22) * mm});
            skLineSegment(sketch, "E318", {"start": v(-12.87, 37.22) * mm, "end": v(-13.26, 37.28) * mm});
            skLineSegment(sketch, "E319", {"start": v(-13.26, 37.28) * mm, "end": v(-13.39, 37.27) * mm});
            skLineSegment(sketch, "E320", {"start": v(-13.39, 37.27) * mm, "end": v(-13.39, 37.27) * mm});
            skLineSegment(sketch, "E321", {"start": v(-18.7, 30.36) * mm, "end": v(-18.07, 30.03) * mm});
            skLineSegment(sketch, "E322", {"start": v(-18.07, 30.03) * mm, "end": v(-16.18, 29.02) * mm});
            skLineSegment(sketch, "E323", {"start": v(-16.18, 29.02) * mm, "end": v(-13.93, 27.75) * mm});
            skLineSegment(sketch, "E324", {"start": v(-13.93, 27.75) * mm, "end": v(-11.93, 26.53) * mm});
            skLineSegment(sketch, "E325", {"start": v(-11.93, 26.53) * mm, "end": v(-10.17, 25.37) * mm});
            skLineSegment(sketch, "E326", {"start": v(-10.17, 25.37) * mm, "end": v(-8.63, 24.27) * mm});
            skLineSegment(sketch, "E327", {"start": v(-8.63, 24.27) * mm, "end": v(-7.3, 23.21) * mm});
            skLineSegment(sketch, "E328", {"start": v(-7.3, 23.21) * mm, "end": v(-6.19, 22.2) * mm});
            skLineSegment(sketch, "E329", {"start": v(-6.19, 22.2) * mm, "end": v(-5.48, 21.5) * mm});
            skLineSegment(sketch, "E330", {"start": v(-5.48, 21.5) * mm, "end": v(-5.25, 21.24) * mm});
            skLineSegment(sketch, "E331", {"start": v(-5.25, 21.24) * mm, "end": v(-5.35, 20.84) * mm});
            skLineSegment(sketch, "E332", {"start": v(-5.35, 20.84) * mm, "end": v(-5.9, 19.7) * mm});
            skLineSegment(sketch, "E333", {"start": v(-5.9, 19.7) * mm, "end": v(-6.9, 18.54) * mm});
            skLineSegment(sketch, "E334", {"start": v(-6.9, 18.54) * mm, "end": v(-8.15, 17.69) * mm});
            skLineSegment(sketch, "E335", {"start": v(-8.15, 17.69) * mm, "end": v(-9.55, 17.1) * mm});
            skLineSegment(sketch, "E336", {"start": v(-9.55, 17.1) * mm, "end": v(-11, 16.75) * mm});
            skLineSegment(sketch, "E337", {"start": v(-11, 16.75) * mm, "end": v(-12.4, 16.56) * mm});
            skLineSegment(sketch, "E338", {"start": v(-12.4, 16.56) * mm, "end": v(-13.64, 16.5) * mm});
            skLineSegment(sketch, "E339", {"start": v(-13.64, 16.5) * mm, "end": v(-14.38, 16.52) * mm});
            skLineSegment(sketch, "E340", {"start": v(-14.38, 16.52) * mm, "end": v(-14.63, 16.53) * mm});
            skLineSegment(sketch, "E341", {"start": v(-14.63, 16.53) * mm, "end": v(-14.55, 16.57) * mm});
            skLineSegment(sketch, "E342", {"start": v(-14.55, 16.57) * mm, "end": v(-14.3, 16.7) * mm});
            skLineSegment(sketch, "E343", {"start": v(-14.3, 16.7) * mm, "end": v(-14.03, 16.9) * mm});
            skLineSegment(sketch, "E344", {"start": v(-14.03, 16.9) * mm, "end": v(-13.81, 17.12) * mm});
            skLineSegment(sketch, "E345", {"start": v(-13.81, 17.12) * mm, "end": v(-13.7, 17.31) * mm});
            skLineSegment(sketch, "E346", {"start": v(-13.7, 17.31) * mm, "end": v(-13.67, 17.38) * mm});
            skLineSegment(sketch, "E347", {"start": v(-13.67, 17.38) * mm, "end": v(-13.8, 17.47) * mm});
            skLineSegment(sketch, "E348", {"start": v(-13.8, 17.47) * mm, "end": v(-14.32, 17.57) * mm});
            skLineSegment(sketch, "E349", {"start": v(-14.32, 17.57) * mm, "end": v(-15.3, 17.65) * mm});
            skLineSegment(sketch, "E350", {"start": v(-15.3, 17.65) * mm, "end": v(-16.44, 17.8) * mm});
            skLineSegment(sketch, "E351", {"start": v(-16.44, 17.8) * mm, "end": v(-17.3, 18.05) * mm});
            skLineSegment(sketch, "E352", {"start": v(-17.3, 18.05) * mm, "end": v(-17.55, 18.2) * mm});
            skLineSegment(sketch, "E353", {"start": v(-17.55, 18.2) * mm, "end": v(-17.46, 18.21) * mm});
            skLineSegment(sketch, "E354", {"start": v(-17.46, 18.21) * mm, "end": v(-17.2, 18.28) * mm});
            skLineSegment(sketch, "E355", {"start": v(-17.2, 18.28) * mm, "end": v(-16.94, 18.39) * mm});
            skLineSegment(sketch, "E356", {"start": v(-16.94, 18.39) * mm, "end": v(-16.72, 18.55) * mm});
            skLineSegment(sketch, "E357", {"start": v(-16.72, 18.55) * mm, "end": v(-16.57, 18.73) * mm});
            skLineSegment(sketch, "E358", {"start": v(-16.57, 18.73) * mm, "end": v(-16.53, 18.8) * mm});
            skLineSegment(sketch, "E359", {"start": v(-16.53, 18.8) * mm, "end": v(-16.78, 18.87) * mm});
            skLineSegment(sketch, "E360", {"start": v(-16.78, 18.87) * mm, "end": v(-17.51, 19.1) * mm});
            skLineSegment(sketch, "E361", {"start": v(-17.51, 19.1) * mm, "end": v(-18.46, 19.42) * mm});
            skLineSegment(sketch, "E362", {"start": v(-18.46, 19.42) * mm, "end": v(-19.32, 19.79) * mm});
            skLineSegment(sketch, "E363", {"start": v(-19.32, 19.79) * mm, "end": v(-19.87, 20.11) * mm});
            skLineSegment(sketch, "E364", {"start": v(-19.87, 20.11) * mm, "end": v(-20.03, 20.24) * mm});
            skLineSegment(sketch, "E365", {"start": v(-20.03, 20.24) * mm, "end": v(-19.95, 20.24) * mm});
            skLineSegment(sketch, "E366", {"start": v(-19.95, 20.24) * mm, "end": v(-19.7, 20.23) * mm});
            skLineSegment(sketch, "E367", {"start": v(-19.7, 20.23) * mm, "end": v(-19.37, 20.24) * mm});
            skLineSegment(sketch, "E368", {"start": v(-19.37, 20.24) * mm, "end": v(-19, 20.33) * mm});
            skLineSegment(sketch, "E369", {"start": v(-19, 20.33) * mm, "end": v(-18.7, 20.48) * mm});
            skLineSegment(sketch, "E370", {"start": v(-18.7, 20.48) * mm, "end": v(-18.6, 20.55) * mm});
            skLineSegment(sketch, "E371", {"start": v(-18.6, 20.55) * mm, "end": v(-18.9, 20.7) * mm});
            skLineSegment(sketch, "E372", {"start": v(-18.9, 20.7) * mm, "end": v(-20.35, 21.46) * mm});
            skLineSegment(sketch, "E373", {"start": v(-20.35, 21.46) * mm, "end": v(-21.72, 22.38) * mm});
            skLineSegment(sketch, "E374", {"start": v(-21.72, 22.38) * mm, "end": v(-21.96, 22.62) * mm});
            skLineSegment(sketch, "E375", {"start": v(-21.96, 22.62) * mm, "end": v(-21.84, 22.62) * mm});
            skLineSegment(sketch, "E376", {"start": v(-21.84, 22.62) * mm, "end": v(-21.5, 22.63) * mm});
            skLineSegment(sketch, "E377", {"start": v(-21.5, 22.63) * mm, "end": v(-21.09, 22.65) * mm});
            skLineSegment(sketch, "E378", {"start": v(-21.09, 22.65) * mm, "end": v(-20.74, 22.72) * mm});
            skLineSegment(sketch, "E379", {"start": v(-20.74, 22.72) * mm, "end": v(-20.56, 22.8) * mm});
            skLineSegment(sketch, "E380", {"start": v(-20.56, 22.8) * mm, "end": v(-20.52, 22.84) * mm});
            skLineSegment(sketch, "E381", {"start": v(-20.52, 22.84) * mm, "end": v(-20.8, 23) * mm});
            skLineSegment(sketch, "E382", {"start": v(-20.8, 23) * mm, "end": v(-22, 23.88) * mm});
            skLineSegment(sketch, "E383", {"start": v(-22, 23.88) * mm, "end": v(-23.03, 24.83) * mm});
            skLineSegment(sketch, "E384", {"start": v(-23.03, 24.83) * mm, "end": v(-23.22, 25.03) * mm});
            skLineSegment(sketch, "E385", {"start": v(-23.22, 25.03) * mm, "end": v(-23.08, 25.01) * mm});
            skLineSegment(sketch, "E386", {"start": v(-23.08, 25.01) * mm, "end": v(-22.68, 24.99) * mm});
            skLineSegment(sketch, "E387", {"start": v(-22.68, 24.99) * mm, "end": v(-22.28, 25) * mm});
            skLineSegment(sketch, "E388", {"start": v(-22.28, 25) * mm, "end": v(-22, 25.06) * mm});
            skLineSegment(sketch, "E389", {"start": v(-22, 25.06) * mm, "end": v(-21.87, 25.13) * mm});
            skLineSegment(sketch, "E390", {"start": v(-21.87, 25.13) * mm, "end": v(-21.82, 25.16) * mm});
            skLineSegment(sketch, "E391", {"start": v(-21.82, 25.16) * mm, "end": v(-21.98, 25.31) * mm});
            skLineSegment(sketch, "E392", {"start": v(-21.98, 25.31) * mm, "end": v(-22.45, 25.76) * mm});
            skLineSegment(sketch, "E393", {"start": v(-22.45, 25.76) * mm, "end": v(-23.1, 26.35) * mm});
            skLineSegment(sketch, "E394", {"start": v(-23.1, 26.35) * mm, "end": v(-23.67, 26.98) * mm});
            skLineSegment(sketch, "E395", {"start": v(-23.67, 26.98) * mm, "end": v(-24.03, 27.5) * mm});
            skLineSegment(sketch, "E396", {"start": v(-24.03, 27.5) * mm, "end": v(-24.12, 27.68) * mm});
            skLineSegment(sketch, "E397", {"start": v(-24.12, 27.68) * mm, "end": v(-24.01, 27.65) * mm});
            skLineSegment(sketch, "E398", {"start": v(-24.01, 27.65) * mm, "end": v(-23.67, 27.55) * mm});
            skLineSegment(sketch, "E399", {"start": v(-23.67, 27.55) * mm, "end": v(-23.24, 27.5) * mm});
            skLineSegment(sketch, "E400", {"start": v(-23.24, 27.5) * mm, "end": v(-22.86, 27.54) * mm});
            skLineSegment(sketch, "E401", {"start": v(-22.86, 27.54) * mm, "end": v(-22.6, 27.65) * mm});
            skLineSegment(sketch, "E402", {"start": v(-22.6, 27.65) * mm, "end": v(-22.52, 27.7) * mm});
            skLineSegment(sketch, "E403", {"start": v(-22.52, 27.7) * mm, "end": v(-22.58, 27.83) * mm});
            skLineSegment(sketch, "E404", {"start": v(-22.58, 27.83) * mm, "end": v(-22.87, 28.14) * mm});
            skLineSegment(sketch, "E405", {"start": v(-22.87, 28.14) * mm, "end": v(-23.43, 28.6) * mm});
            skLineSegment(sketch, "E406", {"start": v(-23.43, 28.6) * mm, "end": v(-24.06, 29.22) * mm});
            skLineSegment(sketch, "E407", {"start": v(-24.06, 29.22) * mm, "end": v(-24.52, 29.87) * mm});
            skLineSegment(sketch, "E408", {"start": v(-24.52, 29.87) * mm, "end": v(-24.63, 30.11) * mm});
            skLineSegment(sketch, "E409", {"start": v(-24.63, 30.11) * mm, "end": v(-24.5, 30.1) * mm});
            skLineSegment(sketch, "E410", {"start": v(-24.5, 30.1) * mm, "end": v(-24.14, 30.07) * mm});
            skLineSegment(sketch, "E411", {"start": v(-24.14, 30.07) * mm, "end": v(-23.7, 30.04) * mm});
            skLineSegment(sketch, "E412", {"start": v(-23.7, 30.04) * mm, "end": v(-23.34, 30.04) * mm});
            skLineSegment(sketch, "E413", {"start": v(-23.34, 30.04) * mm, "end": v(-23.18, 30.08) * mm});
            skLineSegment(sketch, "E414", {"start": v(-23.18, 30.08) * mm, "end": v(-23.14, 30.11) * mm});
            skLineSegment(sketch, "E415", {"start": v(-23.14, 30.11) * mm, "end": v(-23.2, 30.33) * mm});
            skLineSegment(sketch, "E416", {"start": v(-23.2, 30.33) * mm, "end": v(-23.4, 30.95) * mm});
            skLineSegment(sketch, "E417", {"start": v(-23.4, 30.95) * mm, "end": v(-23.73, 31.63) * mm});
            skLineSegment(sketch, "E418", {"start": v(-23.73, 31.63) * mm, "end": v(-24.1, 32.22) * mm});
            skLineSegment(sketch, "E419", {"start": v(-24.1, 32.22) * mm, "end": v(-24.38, 32.63) * mm});
            skLineSegment(sketch, "E420", {"start": v(-24.38, 32.63) * mm, "end": v(-24.48, 32.77) * mm});
            skLineSegment(sketch, "E421", {"start": v(-24.48, 32.77) * mm, "end": v(-24.2, 32.77) * mm});
            skLineSegment(sketch, "E422", {"start": v(-24.2, 32.77) * mm, "end": v(-23.34, 32.78) * mm});
            skLineSegment(sketch, "E423", {"start": v(-23.34, 32.78) * mm, "end": v(-22.2, 32.79) * mm});
            skLineSegment(sketch, "E424", {"start": v(-22.2, 32.79) * mm, "end": v(-21.35, 32.82) * mm});
            skLineSegment(sketch, "E425", {"start": v(-21.35, 32.82) * mm, "end": v(-21.05, 32.88) * mm});
            skLineSegment(sketch, "E426", {"start": v(-21.05, 32.88) * mm, "end": v(-21.92, 33.77) * mm});
            skLineSegment(sketch, "E427", {"start": v(-21.92, 33.77) * mm, "end": v(-21.67, 33.83) * mm});
            skLineSegment(sketch, "E428", {"start": v(-21.67, 33.83) * mm, "end": v(-20.9, 33.9) * mm});
            skLineSegment(sketch, "E429", {"start": v(-20.9, 33.9) * mm, "end": v(-19.9, 33.83) * mm});
            skLineSegment(sketch, "E430", {"start": v(-19.9, 33.83) * mm, "end": v(-18.96, 33.63) * mm});
            skLineSegment(sketch, "E431", {"start": v(-18.96, 33.63) * mm, "end": v(-18.34, 33.45) * mm});
            skLineSegment(sketch, "E432", {"start": v(-18.34, 33.45) * mm, "end": v(-18.13, 33.39) * mm});
            skLineSegment(sketch, "E433", {"start": v(-18.13, 33.39) * mm, "end": v(-18.07, 33.44) * mm});
            skLineSegment(sketch, "E434", {"start": v(-18.07, 33.44) * mm, "end": v(-17.95, 33.68) * mm});
            skLineSegment(sketch, "E435", {"start": v(-17.95, 33.68) * mm, "end": v(-18.04, 34) * mm});
            skLineSegment(sketch, "E436", {"start": v(-18.04, 34) * mm, "end": v(-18.31, 34.32) * mm});
            skLineSegment(sketch, "E437", {"start": v(-18.31, 34.32) * mm, "end": v(-18.6, 34.59) * mm});
            skLineSegment(sketch, "E438", {"start": v(-18.6, 34.59) * mm, "end": v(-18.7, 34.67) * mm});
            skLineSegment(sketch, "E439", {"start": v(-18.7, 34.67) * mm, "end": v(-18.4, 34.63) * mm});
            skLineSegment(sketch, "E440", {"start": v(-18.4, 34.63) * mm, "end": v(-17.04, 34.35) * mm});
            skLineSegment(sketch, "E441", {"start": v(-17.04, 34.35) * mm, "end": v(-15.77, 33.97) * mm});
            skLineSegment(sketch, "E442", {"start": v(-15.77, 33.97) * mm, "end": v(-15.53, 33.88) * mm});
            skLineSegment(sketch, "E443", {"start": v(-15.53, 33.88) * mm, "end": v(-15.47, 33.94) * mm});
            skLineSegment(sketch, "E444", {"start": v(-15.47, 33.94) * mm, "end": v(-15.38, 34.22) * mm});
            skLineSegment(sketch, "E445", {"start": v(-15.38, 34.22) * mm, "end": v(-15.56, 34.57) * mm});
            skLineSegment(sketch, "E446", {"start": v(-15.56, 34.57) * mm, "end": v(-15.91, 34.9) * mm});
            skLineSegment(sketch, "E447", {"start": v(-15.91, 34.9) * mm, "end": v(-16.19, 35.16) * mm});
            skLineSegment(sketch, "E448", {"start": v(-16.19, 35.16) * mm, "end": v(-16.27, 35.25) * mm});
            skLineSegment(sketch, "E449", {"start": v(-16.27, 35.25) * mm, "end": v(-15.97, 35.2) * mm});
            skLineSegment(sketch, "E450", {"start": v(-15.97, 35.2) * mm, "end": v(-15.1, 34.97) * mm});
            skLineSegment(sketch, "E451", {"start": v(-15.1, 34.97) * mm, "end": v(-14.22, 34.66) * mm});
            skLineSegment(sketch, "E452", {"start": v(-14.22, 34.66) * mm, "end": v(-13.54, 34.31) * mm});
            skLineSegment(sketch, "E453", {"start": v(-13.54, 34.31) * mm, "end": v(-13.1, 34.05) * mm});
            skLineSegment(sketch, "E454", {"start": v(-13.1, 34.05) * mm, "end": v(-12.95, 33.95) * mm});
            skLineSegment(sketch, "E455", {"start": v(-12.95, 33.95) * mm, "end": v(-12.88, 34.03) * mm});
            skLineSegment(sketch, "E456", {"start": v(-12.88, 34.03) * mm, "end": v(-12.72, 34.34) * mm});
            skLineSegment(sketch, "E457", {"start": v(-12.72, 34.34) * mm, "end": v(-12.78, 34.7) * mm});
            skLineSegment(sketch, "E458", {"start": v(-12.78, 34.7) * mm, "end": v(-13, 35.04) * mm});
            skLineSegment(sketch, "E459", {"start": v(-13, 35.04) * mm, "end": v(-13.22, 35.3) * mm});
            skLineSegment(sketch, "E460", {"start": v(-13.22, 35.3) * mm, "end": v(-13.3, 35.39) * mm});
            skLineSegment(sketch, "E461", {"start": v(-13.3, 35.39) * mm, "end": v(-13.06, 35.3) * mm});
            skLineSegment(sketch, "E462", {"start": v(-13.06, 35.3) * mm, "end": v(-12.39, 34.98) * mm});
            skLineSegment(sketch, "E463", {"start": v(-12.39, 34.98) * mm, "end": v(-11.67, 34.54) * mm});
            skLineSegment(sketch, "E464", {"start": v(-11.67, 34.54) * mm, "end": v(-11.06, 34.08) * mm});
            skLineSegment(sketch, "E465", {"start": v(-11.06, 34.08) * mm, "end": v(-10.64, 33.72) * mm});
            skLineSegment(sketch, "E466", {"start": v(-10.64, 33.72) * mm, "end": v(-10.5, 33.6) * mm});
            skLineSegment(sketch, "E467", {"start": v(-10.5, 33.6) * mm, "end": v(-10.46, 33.66) * mm});
            skLineSegment(sketch, "E468", {"start": v(-10.46, 33.66) * mm, "end": v(-10.3, 33.84) * mm});
            skLineSegment(sketch, "E469", {"start": v(-10.3, 33.84) * mm, "end": v(-10.15, 34.12) * mm});
            skLineSegment(sketch, "E470", {"start": v(-10.15, 34.12) * mm, "end": v(-10.13, 34.48) * mm});
            skLineSegment(sketch, "E471", {"start": v(-10.13, 34.48) * mm, "end": v(-10.27, 34.87) * mm});
            skLineSegment(sketch, "E472", {"start": v(-10.27, 34.87) * mm, "end": v(-10.34, 34.99) * mm});
            skLineSegment(sketch, "E473", {"start": v(-10.34, 34.99) * mm, "end": v(-10.1, 34.85) * mm});
            skLineSegment(sketch, "E474", {"start": v(-10.1, 34.85) * mm, "end": v(-9.07, 34.09) * mm});
            skLineSegment(sketch, "E475", {"start": v(-9.07, 34.09) * mm, "end": v(-8.25, 33.23) * mm});
            skLineSegment(sketch, "E476", {"start": v(-8.25, 33.23) * mm, "end": v(-8.11, 33.05) * mm});
            skLineSegment(sketch, "E477", {"start": v(-8.11, 33.05) * mm, "end": v(-8.02, 33.1) * mm});
            skLineSegment(sketch, "E478", {"start": v(-8.02, 33.1) * mm, "end": v(-7.8, 33.36) * mm});
            skLineSegment(sketch, "E479", {"start": v(-7.8, 33.36) * mm, "end": v(-7.71, 33.7) * mm});
            skLineSegment(sketch, "E480", {"start": v(-7.71, 33.7) * mm, "end": v(-7.73, 34.06) * mm});
            skLineSegment(sketch, "E481", {"start": v(-7.73, 34.06) * mm, "end": v(-7.76, 34.33) * mm});
            skLineSegment(sketch, "E482", {"start": v(-7.76, 34.33) * mm, "end": v(-7.76, 34.42) * mm});
            skLineSegment(sketch, "E483", {"start": v(-7.76, 34.42) * mm, "end": v(-7.5, 34.22) * mm});
            skLineSegment(sketch, "E484", {"start": v(-7.5, 34.22) * mm, "end": v(-6.47, 33.18) * mm});
            skLineSegment(sketch, "E485", {"start": v(-6.47, 33.18) * mm, "end": v(-5.54, 32.11) * mm});
            skLineSegment(sketch, "E486", {"start": v(-5.54, 32.11) * mm, "end": v(-5.34, 31.9) * mm});
            skLineSegment(sketch, "E487", {"start": v(-5.34, 31.9) * mm, "end": v(-5.3, 31.93) * mm});
            skLineSegment(sketch, "E488", {"start": v(-5.3, 31.93) * mm, "end": v(-5.12, 32.27) * mm});
            skLineSegment(sketch, "E489", {"start": v(-5.12, 32.27) * mm, "end": v(-4.96, 32.86) * mm});
            skLineSegment(sketch, "E490", {"start": v(-4.96, 32.86) * mm, "end": v(-4.93, 33.01) * mm});
            skLineSegment(sketch, "E491", {"start": v(-4.93, 33.01) * mm, "end": v(-4.69, 32.77) * mm});
            skLineSegment(sketch, "E492", {"start": v(-4.69, 32.77) * mm, "end": v(-4, 32) * mm});
            skLineSegment(sketch, "E493", {"start": v(-4, 32) * mm, "end": v(-3.1, 30.73) * mm});
            skLineSegment(sketch, "E494", {"start": v(-3.1, 30.73) * mm, "end": v(-2.32, 29.3) * mm});
            skLineSegment(sketch, "E495", {"start": v(-2.32, 29.3) * mm, "end": v(-1.77, 27.79) * mm});
            skLineSegment(sketch, "E496", {"start": v(-1.77, 27.79) * mm, "end": v(-1.56, 26.27) * mm});
            skLineSegment(sketch, "E497", {"start": v(-1.56, 26.27) * mm, "end": v(-1.8, 24.84) * mm});
            skLineSegment(sketch, "E498", {"start": v(-1.8, 24.84) * mm, "end": v(-2.6, 23.58) * mm});
            skLineSegment(sketch, "E499", {"start": v(-2.6, 23.58) * mm, "end": v(-3.67, 22.75) * mm});
            skLineSegment(sketch, "E500", {"start": v(-3.67, 22.75) * mm, "end": v(-4.06, 22.56) * mm});
            skLineSegment(sketch, "E501", {"start": v(-4.06, 22.56) * mm, "end": v(-4.85, 23.2) * mm});
            skLineSegment(sketch, "E502", {"start": v(-4.85, 23.2) * mm, "end": v(-7.33, 24.96) * mm});
            skLineSegment(sketch, "E503", {"start": v(-7.33, 24.96) * mm, "end": v(-10.88, 27.04) * mm});
            skLineSegment(sketch, "E504", {"start": v(-10.88, 27.04) * mm, "end": v(-14.68, 28.83) * mm});
            skLineSegment(sketch, "E505", {"start": v(-14.68, 28.83) * mm, "end": v(-17.68, 30.01) * mm});
            skLineSegment(sketch, "E506", {"start": v(-17.68, 30.01) * mm, "end": v(-18.7, 30.36) * mm});
            skLineSegment(sketch, "E507", {"start": v(-18.7, 30.36) * mm, "end": v(-18.7, 30.36) * mm});
            skLineSegment(sketch, "E508", {"start": v(18.86, 30.36) * mm, "end": v(18.22, 30.03) * mm});
            skLineSegment(sketch, "E509", {"start": v(18.22, 30.03) * mm, "end": v(16.34, 29.02) * mm});
            skLineSegment(sketch, "E510", {"start": v(16.34, 29.02) * mm, "end": v(14.09, 27.75) * mm});
            skLineSegment(sketch, "E511", {"start": v(14.09, 27.75) * mm, "end": v(12.09, 26.53) * mm});
            skLineSegment(sketch, "E512", {"start": v(12.09, 26.53) * mm, "end": v(10.33, 25.37) * mm});
            skLineSegment(sketch, "E513", {"start": v(10.33, 25.37) * mm, "end": v(8.79, 24.27) * mm});
            skLineSegment(sketch, "E514", {"start": v(8.79, 24.27) * mm, "end": v(7.47, 23.21) * mm});
            skLineSegment(sketch, "E515", {"start": v(7.47, 23.21) * mm, "end": v(6.35, 22.2) * mm});
            skLineSegment(sketch, "E516", {"start": v(6.35, 22.2) * mm, "end": v(5.63, 21.5) * mm});
            skLineSegment(sketch, "E517", {"start": v(5.63, 21.5) * mm, "end": v(5.41, 21.24) * mm});
            skLineSegment(sketch, "E518", {"start": v(5.41, 21.24) * mm, "end": v(5.51, 20.84) * mm});
            skLineSegment(sketch, "E519", {"start": v(5.51, 20.84) * mm, "end": v(6.05, 19.7) * mm});
            skLineSegment(sketch, "E520", {"start": v(6.05, 19.7) * mm, "end": v(7.05, 18.54) * mm});
            skLineSegment(sketch, "E521", {"start": v(7.05, 18.54) * mm, "end": v(8.3, 17.69) * mm});
            skLineSegment(sketch, "E522", {"start": v(8.3, 17.69) * mm, "end": v(9.7, 17.1) * mm});
            skLineSegment(sketch, "E523", {"start": v(9.7, 17.1) * mm, "end": v(11.16, 16.75) * mm});
            skLineSegment(sketch, "E524", {"start": v(11.16, 16.75) * mm, "end": v(12.56, 16.56) * mm});
            skLineSegment(sketch, "E525", {"start": v(12.56, 16.56) * mm, "end": v(13.8, 16.5) * mm});
            skLineSegment(sketch, "E526", {"start": v(13.8, 16.5) * mm, "end": v(14.54, 16.52) * mm});
            skLineSegment(sketch, "E527", {"start": v(14.54, 16.52) * mm, "end": v(14.79, 16.53) * mm});
            skLineSegment(sketch, "E528", {"start": v(14.79, 16.53) * mm, "end": v(14.7, 16.57) * mm});
            skLineSegment(sketch, "E529", {"start": v(14.7, 16.57) * mm, "end": v(14.47, 16.7) * mm});
            skLineSegment(sketch, "E530", {"start": v(14.47, 16.7) * mm, "end": v(14.2, 16.9) * mm});
            skLineSegment(sketch, "E531", {"start": v(14.2, 16.9) * mm, "end": v(13.97, 17.12) * mm});
            skLineSegment(sketch, "E532", {"start": v(13.97, 17.12) * mm, "end": v(13.85, 17.31) * mm});
            skLineSegment(sketch, "E533", {"start": v(13.85, 17.31) * mm, "end": v(13.83, 17.38) * mm});
            skLineSegment(sketch, "E534", {"start": v(13.83, 17.38) * mm, "end": v(13.96, 17.47) * mm});
            skLineSegment(sketch, "E535", {"start": v(13.96, 17.47) * mm, "end": v(14.48, 17.57) * mm});
            skLineSegment(sketch, "E536", {"start": v(14.48, 17.57) * mm, "end": v(15.46, 17.65) * mm});
            skLineSegment(sketch, "E537", {"start": v(15.46, 17.65) * mm, "end": v(16.6, 17.8) * mm});
            skLineSegment(sketch, "E538", {"start": v(16.6, 17.8) * mm, "end": v(17.46, 18.05) * mm});
            skLineSegment(sketch, "E539", {"start": v(17.46, 18.05) * mm, "end": v(17.7, 18.2) * mm});
            skLineSegment(sketch, "E540", {"start": v(17.7, 18.2) * mm, "end": v(17.62, 18.21) * mm});
            skLineSegment(sketch, "E541", {"start": v(17.62, 18.21) * mm, "end": v(17.36, 18.28) * mm});
            skLineSegment(sketch, "E542", {"start": v(17.36, 18.28) * mm, "end": v(17.1, 18.39) * mm});
            skLineSegment(sketch, "E543", {"start": v(17.1, 18.39) * mm, "end": v(16.88, 18.55) * mm});
            skLineSegment(sketch, "E544", {"start": v(16.88, 18.55) * mm, "end": v(16.73, 18.73) * mm});
            skLineSegment(sketch, "E545", {"start": v(16.73, 18.73) * mm, "end": v(16.7, 18.8) * mm});
            skLineSegment(sketch, "E546", {"start": v(16.7, 18.8) * mm, "end": v(16.94, 18.87) * mm});
            skLineSegment(sketch, "E547", {"start": v(16.94, 18.87) * mm, "end": v(17.67, 19.1) * mm});
            skLineSegment(sketch, "E548", {"start": v(17.67, 19.1) * mm, "end": v(18.62, 19.42) * mm});
            skLineSegment(sketch, "E549", {"start": v(18.62, 19.42) * mm, "end": v(19.48, 19.79) * mm});
            skLineSegment(sketch, "E550", {"start": v(19.48, 19.79) * mm, "end": v(20.03, 20.11) * mm});
            skLineSegment(sketch, "E551", {"start": v(20.03, 20.11) * mm, "end": v(20.2, 20.24) * mm});
            skLineSegment(sketch, "E552", {"start": v(20.2, 20.24) * mm, "end": v(20.11, 20.24) * mm});
            skLineSegment(sketch, "E553", {"start": v(20.11, 20.24) * mm, "end": v(19.87, 20.23) * mm});
            skLineSegment(sketch, "E554", {"start": v(19.87, 20.23) * mm, "end": v(19.53, 20.24) * mm});
            skLineSegment(sketch, "E555", {"start": v(19.53, 20.24) * mm, "end": v(19.17, 20.33) * mm});
            skLineSegment(sketch, "E556", {"start": v(19.17, 20.33) * mm, "end": v(18.86, 20.48) * mm});
            skLineSegment(sketch, "E557", {"start": v(18.86, 20.48) * mm, "end": v(18.76, 20.55) * mm});
            skLineSegment(sketch, "E558", {"start": v(18.76, 20.55) * mm, "end": v(19.05, 20.7) * mm});
            skLineSegment(sketch, "E559", {"start": v(19.05, 20.7) * mm, "end": v(20.51, 21.46) * mm});
            skLineSegment(sketch, "E560", {"start": v(20.51, 21.46) * mm, "end": v(21.88, 22.38) * mm});
            skLineSegment(sketch, "E561", {"start": v(21.88, 22.38) * mm, "end": v(22.12, 22.62) * mm});
            skLineSegment(sketch, "E562", {"start": v(22.12, 22.62) * mm, "end": v(22, 22.62) * mm});
            skLineSegment(sketch, "E563", {"start": v(22, 22.62) * mm, "end": v(21.67, 22.63) * mm});
            skLineSegment(sketch, "E564", {"start": v(21.67, 22.63) * mm, "end": v(21.25, 22.65) * mm});
            skLineSegment(sketch, "E565", {"start": v(21.25, 22.65) * mm, "end": v(20.9, 22.72) * mm});
            skLineSegment(sketch, "E566", {"start": v(20.9, 22.72) * mm, "end": v(20.72, 22.8) * mm});
            skLineSegment(sketch, "E567", {"start": v(20.72, 22.8) * mm, "end": v(20.68, 22.84) * mm});
            skLineSegment(sketch, "E568", {"start": v(20.68, 22.84) * mm, "end": v(20.95, 23) * mm});
            skLineSegment(sketch, "E569", {"start": v(20.95, 23) * mm, "end": v(22.15, 23.88) * mm});
            skLineSegment(sketch, "E570", {"start": v(22.15, 23.88) * mm, "end": v(23.2, 24.83) * mm});
            skLineSegment(sketch, "E571", {"start": v(23.2, 24.83) * mm, "end": v(23.38, 25.03) * mm});
            skLineSegment(sketch, "E572", {"start": v(23.38, 25.03) * mm, "end": v(23.24, 25.01) * mm});
            skLineSegment(sketch, "E573", {"start": v(23.24, 25.01) * mm, "end": v(22.83, 24.99) * mm});
            skLineSegment(sketch, "E574", {"start": v(22.83, 24.99) * mm, "end": v(22.44, 25) * mm});
            skLineSegment(sketch, "E575", {"start": v(22.44, 25) * mm, "end": v(22.17, 25.06) * mm});
            skLineSegment(sketch, "E576", {"start": v(22.17, 25.06) * mm, "end": v(22.03, 25.13) * mm});
            skLineSegment(sketch, "E577", {"start": v(22.03, 25.13) * mm, "end": v(21.98, 25.16) * mm});
            skLineSegment(sketch, "E578", {"start": v(21.98, 25.16) * mm, "end": v(22.14, 25.31) * mm});
            skLineSegment(sketch, "E579", {"start": v(22.14, 25.31) * mm, "end": v(22.61, 25.76) * mm});
            skLineSegment(sketch, "E580", {"start": v(22.61, 25.76) * mm, "end": v(23.25, 26.35) * mm});
            skLineSegment(sketch, "E581", {"start": v(23.25, 26.35) * mm, "end": v(23.83, 26.98) * mm});
            skLineSegment(sketch, "E582", {"start": v(23.83, 26.98) * mm, "end": v(24.2, 27.5) * mm});
            skLineSegment(sketch, "E583", {"start": v(24.2, 27.5) * mm, "end": v(24.28, 27.68) * mm});
            skLineSegment(sketch, "E584", {"start": v(24.28, 27.68) * mm, "end": v(24.17, 27.65) * mm});
            skLineSegment(sketch, "E585", {"start": v(24.17, 27.65) * mm, "end": v(23.83, 27.55) * mm});
            skLineSegment(sketch, "E586", {"start": v(23.83, 27.55) * mm, "end": v(23.4, 27.5) * mm});
            skLineSegment(sketch, "E587", {"start": v(23.4, 27.5) * mm, "end": v(23.02, 27.54) * mm});
            skLineSegment(sketch, "E588", {"start": v(23.02, 27.54) * mm, "end": v(22.75, 27.65) * mm});
            skLineSegment(sketch, "E589", {"start": v(22.75, 27.65) * mm, "end": v(22.68, 27.7) * mm});
            skLineSegment(sketch, "E590", {"start": v(22.68, 27.7) * mm, "end": v(22.74, 27.83) * mm});
            skLineSegment(sketch, "E591", {"start": v(22.74, 27.83) * mm, "end": v(23.03, 28.14) * mm});
            skLineSegment(sketch, "E592", {"start": v(23.03, 28.14) * mm, "end": v(23.59, 28.6) * mm});
            skLineSegment(sketch, "E593", {"start": v(23.59, 28.6) * mm, "end": v(24.22, 29.22) * mm});
            skLineSegment(sketch, "E594", {"start": v(24.22, 29.22) * mm, "end": v(24.68, 29.87) * mm});
            skLineSegment(sketch, "E595", {"start": v(24.68, 29.87) * mm, "end": v(24.8, 30.11) * mm});
            skLineSegment(sketch, "E596", {"start": v(24.8, 30.11) * mm, "end": v(24.67, 30.1) * mm});
            skLineSegment(sketch, "E597", {"start": v(24.67, 30.1) * mm, "end": v(24.3, 30.07) * mm});
            skLineSegment(sketch, "E598", {"start": v(24.3, 30.07) * mm, "end": v(23.85, 30.04) * mm});
            skLineSegment(sketch, "E599", {"start": v(23.85, 30.04) * mm, "end": v(23.5, 30.04) * mm});
            skLineSegment(sketch, "E600", {"start": v(23.5, 30.04) * mm, "end": v(23.33, 30.08) * mm});
            skLineSegment(sketch, "E601", {"start": v(23.33, 30.08) * mm, "end": v(23.3, 30.11) * mm});
            skLineSegment(sketch, "E602", {"start": v(23.3, 30.11) * mm, "end": v(23.35, 30.33) * mm});
            skLineSegment(sketch, "E603", {"start": v(23.35, 30.33) * mm, "end": v(23.57, 30.95) * mm});
            skLineSegment(sketch, "E604", {"start": v(23.57, 30.95) * mm, "end": v(23.9, 31.63) * mm});
            skLineSegment(sketch, "E605", {"start": v(23.9, 31.63) * mm, "end": v(24.26, 32.22) * mm});
            skLineSegment(sketch, "E606", {"start": v(24.26, 32.22) * mm, "end": v(24.54, 32.63) * mm});
            skLineSegment(sketch, "E607", {"start": v(24.54, 32.63) * mm, "end": v(24.64, 32.77) * mm});
            skLineSegment(sketch, "E608", {"start": v(24.64, 32.77) * mm, "end": v(24.35, 32.77) * mm});
            skLineSegment(sketch, "E609", {"start": v(24.35, 32.77) * mm, "end": v(23.5, 32.78) * mm});
            skLineSegment(sketch, "E610", {"start": v(23.5, 32.78) * mm, "end": v(22.36, 32.79) * mm});
            skLineSegment(sketch, "E611", {"start": v(22.36, 32.79) * mm, "end": v(21.5, 32.82) * mm});
            skLineSegment(sketch, "E612", {"start": v(21.5, 32.82) * mm, "end": v(21.21, 32.88) * mm});
            skLineSegment(sketch, "E613", {"start": v(21.21, 32.88) * mm, "end": v(22.08, 33.77) * mm});
            skLineSegment(sketch, "E614", {"start": v(22.08, 33.77) * mm, "end": v(21.83, 33.83) * mm});
            skLineSegment(sketch, "E615", {"start": v(21.83, 33.83) * mm, "end": v(21.05, 33.9) * mm});
            skLineSegment(sketch, "E616", {"start": v(21.05, 33.9) * mm, "end": v(20.05, 33.84) * mm});
            skLineSegment(sketch, "E617", {"start": v(20.05, 33.84) * mm, "end": v(19.12, 33.63) * mm});
            skLineSegment(sketch, "E618", {"start": v(19.12, 33.63) * mm, "end": v(18.5, 33.45) * mm});
            skLineSegment(sketch, "E619", {"start": v(18.5, 33.45) * mm, "end": v(18.3, 33.39) * mm});
            skLineSegment(sketch, "E620", {"start": v(18.3, 33.39) * mm, "end": v(18.23, 33.44) * mm});
            skLineSegment(sketch, "E621", {"start": v(18.23, 33.44) * mm, "end": v(18.11, 33.68) * mm});
            skLineSegment(sketch, "E622", {"start": v(18.11, 33.68) * mm, "end": v(18.2, 34) * mm});
            skLineSegment(sketch, "E623", {"start": v(18.2, 34) * mm, "end": v(18.47, 34.33) * mm});
            skLineSegment(sketch, "E624", {"start": v(18.47, 34.33) * mm, "end": v(18.76, 34.59) * mm});
            skLineSegment(sketch, "E625", {"start": v(18.76, 34.59) * mm, "end": v(18.86, 34.67) * mm});
            skLineSegment(sketch, "E626", {"start": v(18.86, 34.67) * mm, "end": v(18.57, 34.63) * mm});
            skLineSegment(sketch, "E627", {"start": v(18.57, 34.63) * mm, "end": v(17.2, 34.35) * mm});
            skLineSegment(sketch, "E628", {"start": v(17.2, 34.35) * mm, "end": v(15.93, 33.97) * mm});
            skLineSegment(sketch, "E629", {"start": v(15.93, 33.97) * mm, "end": v(15.7, 33.88) * mm});
            skLineSegment(sketch, "E630", {"start": v(15.7, 33.88) * mm, "end": v(15.63, 33.94) * mm});
            skLineSegment(sketch, "E631", {"start": v(15.63, 33.94) * mm, "end": v(15.54, 34.22) * mm});
            skLineSegment(sketch, "E632", {"start": v(15.54, 34.22) * mm, "end": v(15.72, 34.57) * mm});
            skLineSegment(sketch, "E633", {"start": v(15.72, 34.57) * mm, "end": v(16.07, 34.91) * mm});
            skLineSegment(sketch, "E634", {"start": v(16.07, 34.91) * mm, "end": v(16.35, 35.16) * mm});
            skLineSegment(sketch, "E635", {"start": v(16.35, 35.16) * mm, "end": v(16.43, 35.25) * mm});
            skLineSegment(sketch, "E636", {"start": v(16.43, 35.25) * mm, "end": v(16.13, 35.2) * mm});
            skLineSegment(sketch, "E637", {"start": v(16.13, 35.2) * mm, "end": v(15.26, 34.98) * mm});
            skLineSegment(sketch, "E638", {"start": v(15.26, 34.98) * mm, "end": v(14.38, 34.66) * mm});
            skLineSegment(sketch, "E639", {"start": v(14.38, 34.66) * mm, "end": v(13.7, 34.31) * mm});
            skLineSegment(sketch, "E640", {"start": v(13.7, 34.31) * mm, "end": v(13.26, 34.05) * mm});
            skLineSegment(sketch, "E641", {"start": v(13.26, 34.05) * mm, "end": v(13.11, 33.95) * mm});
            skLineSegment(sketch, "E642", {"start": v(13.11, 33.95) * mm, "end": v(13.04, 34.03) * mm});
            skLineSegment(sketch, "E643", {"start": v(13.04, 34.03) * mm, "end": v(12.88, 34.34) * mm});
            skLineSegment(sketch, "E644", {"start": v(12.88, 34.34) * mm, "end": v(12.94, 34.7) * mm});
            skLineSegment(sketch, "E645", {"start": v(12.94, 34.7) * mm, "end": v(13.17, 35.04) * mm});
            skLineSegment(sketch, "E646", {"start": v(13.17, 35.04) * mm, "end": v(13.38, 35.3) * mm});
            skLineSegment(sketch, "E647", {"start": v(13.38, 35.3) * mm, "end": v(13.45, 35.39) * mm});
            skLineSegment(sketch, "E648", {"start": v(13.45, 35.39) * mm, "end": v(13.22, 35.3) * mm});
            skLineSegment(sketch, "E649", {"start": v(13.22, 35.3) * mm, "end": v(12.55, 34.98) * mm});
            skLineSegment(sketch, "E650", {"start": v(12.55, 34.98) * mm, "end": v(11.83, 34.54) * mm});
            skLineSegment(sketch, "E651", {"start": v(11.83, 34.54) * mm, "end": v(11.22, 34.08) * mm});
            skLineSegment(sketch, "E652", {"start": v(11.22, 34.08) * mm, "end": v(10.8, 33.72) * mm});
            skLineSegment(sketch, "E653", {"start": v(10.8, 33.72) * mm, "end": v(10.67, 33.6) * mm});
            skLineSegment(sketch, "E654", {"start": v(10.67, 33.6) * mm, "end": v(10.62, 33.66) * mm});
            skLineSegment(sketch, "E655", {"start": v(10.62, 33.66) * mm, "end": v(10.47, 33.84) * mm});
            skLineSegment(sketch, "E656", {"start": v(10.47, 33.84) * mm, "end": v(10.31, 34.12) * mm});
            skLineSegment(sketch, "E657", {"start": v(10.31, 34.12) * mm, "end": v(10.3, 34.48) * mm});
            skLineSegment(sketch, "E658", {"start": v(10.3, 34.48) * mm, "end": v(10.43, 34.87) * mm});
            skLineSegment(sketch, "E659", {"start": v(10.43, 34.87) * mm, "end": v(10.5, 35) * mm});
            skLineSegment(sketch, "E660", {"start": v(10.5, 35) * mm, "end": v(10.26, 34.85) * mm});
            skLineSegment(sketch, "E661", {"start": v(10.26, 34.85) * mm, "end": v(9.22, 34.09) * mm});
            skLineSegment(sketch, "E662", {"start": v(9.22, 34.09) * mm, "end": v(8.4, 33.23) * mm});
            skLineSegment(sketch, "E663", {"start": v(8.4, 33.23) * mm, "end": v(8.27, 33.05) * mm});
            skLineSegment(sketch, "E664", {"start": v(8.27, 33.05) * mm, "end": v(8.18, 33.1) * mm});
            skLineSegment(sketch, "E665", {"start": v(8.18, 33.1) * mm, "end": v(7.97, 33.36) * mm});
            skLineSegment(sketch, "E666", {"start": v(7.97, 33.36) * mm, "end": v(7.87, 33.7) * mm});
            skLineSegment(sketch, "E667", {"start": v(7.87, 33.7) * mm, "end": v(7.89, 34.06) * mm});
            skLineSegment(sketch, "E668", {"start": v(7.89, 34.06) * mm, "end": v(7.92, 34.33) * mm});
            skLineSegment(sketch, "E669", {"start": v(7.92, 34.33) * mm, "end": v(7.92, 34.43) * mm});
            skLineSegment(sketch, "E670", {"start": v(7.92, 34.43) * mm, "end": v(7.67, 34.22) * mm});
            skLineSegment(sketch, "E671", {"start": v(7.67, 34.22) * mm, "end": v(6.63, 33.18) * mm});
            skLineSegment(sketch, "E672", {"start": v(6.63, 33.18) * mm, "end": v(5.7, 32.11) * mm});
            skLineSegment(sketch, "E673", {"start": v(5.7, 32.11) * mm, "end": v(5.5, 31.9) * mm});
            skLineSegment(sketch, "E674", {"start": v(5.5, 31.9) * mm, "end": v(5.47, 31.93) * mm});
            skLineSegment(sketch, "E675", {"start": v(5.47, 31.93) * mm, "end": v(5.28, 32.27) * mm});
            skLineSegment(sketch, "E676", {"start": v(5.28, 32.27) * mm, "end": v(5.12, 32.86) * mm});
            skLineSegment(sketch, "E677", {"start": v(5.12, 32.86) * mm, "end": v(5.1, 33.01) * mm});
            skLineSegment(sketch, "E678", {"start": v(5.1, 33.01) * mm, "end": v(4.84, 32.77) * mm});
            skLineSegment(sketch, "E679", {"start": v(4.84, 32.77) * mm, "end": v(4.17, 32) * mm});
            skLineSegment(sketch, "E680", {"start": v(4.17, 32) * mm, "end": v(3.26, 30.73) * mm});
            skLineSegment(sketch, "E681", {"start": v(3.26, 30.73) * mm, "end": v(2.48, 29.3) * mm});
            skLineSegment(sketch, "E682", {"start": v(2.48, 29.3) * mm, "end": v(1.93, 27.79) * mm});
            skLineSegment(sketch, "E683", {"start": v(1.93, 27.79) * mm, "end": v(1.72, 26.27) * mm});
            skLineSegment(sketch, "E684", {"start": v(1.72, 26.27) * mm, "end": v(1.96, 24.84) * mm});
            skLineSegment(sketch, "E685", {"start": v(1.96, 24.84) * mm, "end": v(2.76, 23.58) * mm});
            skLineSegment(sketch, "E686", {"start": v(2.76, 23.58) * mm, "end": v(3.83, 22.75) * mm});
            skLineSegment(sketch, "E687", {"start": v(3.83, 22.75) * mm, "end": v(4.22, 22.56) * mm});
            skLineSegment(sketch, "E688", {"start": v(4.22, 22.56) * mm, "end": v(5, 23.2) * mm});
            skLineSegment(sketch, "E689", {"start": v(5, 23.2) * mm, "end": v(7.5, 24.96) * mm});
            skLineSegment(sketch, "E690", {"start": v(7.5, 24.96) * mm, "end": v(11.04, 27.04) * mm});
            skLineSegment(sketch, "E691", {"start": v(11.04, 27.04) * mm, "end": v(14.83, 28.83) * mm});
            skLineSegment(sketch, "E692", {"start": v(14.83, 28.83) * mm, "end": v(17.84, 30.01) * mm});
            skLineSegment(sketch, "E693", {"start": v(17.84, 30.01) * mm, "end": v(18.86, 30.36) * mm});
            skLineSegment(sketch, "E694", {"start": v(18.86, 30.36) * mm, "end": v(18.86, 30.36) * mm});
            skLineSegment(sketch, "E695", {"start": v(8.65, -16.76) * mm, "end": v(8.65, -17.14) * mm});
            skLineSegment(sketch, "E696", {"start": v(8.65, -17.14) * mm, "end": v(8.5, -18.3) * mm});
            skLineSegment(sketch, "E697", {"start": v(8.5, -18.3) * mm, "end": v(8.02, -19.76) * mm});
            skLineSegment(sketch, "E698", {"start": v(8.02, -19.76) * mm, "end": v(7.24, -21.11) * mm});
            skLineSegment(sketch, "E699", {"start": v(7.24, -21.11) * mm, "end": v(6.47, -22.04) * mm});
            skLineSegment(sketch, "E700", {"start": v(6.47, -22.04) * mm, "end": v(6.18, -22.31) * mm});
            skLineSegment(sketch, "E701", {"start": v(6.18, -22.31) * mm, "end": v(5.89, -22.59) * mm});
            skLineSegment(sketch, "E702", {"start": v(5.89, -22.59) * mm, "end": v(4.9, -23.3) * mm});
            skLineSegment(sketch, "E703", {"start": v(4.9, -23.3) * mm, "end": v(3.43, -24.02) * mm});
            skLineSegment(sketch, "E704", {"start": v(3.43, -24.02) * mm, "end": v(1.84, -24.46) * mm});
            skLineSegment(sketch, "E705", {"start": v(1.84, -24.46) * mm, "end": v(0.59, -24.62) * mm});
            skLineSegment(sketch, "E706", {"start": v(0.59, -24.62) * mm, "end": v(0.17, -24.62) * mm});
            skLineSegment(sketch, "E707", {"start": v(0.17, -24.62) * mm, "end": v(-0.24, -24.62) * mm});
            skLineSegment(sketch, "E708", {"start": v(-0.24, -24.62) * mm, "end": v(-1.5, -24.46) * mm});
            skLineSegment(sketch, "E709", {"start": v(-1.5, -24.46) * mm, "end": v(-3.08, -24.02) * mm});
            skLineSegment(sketch, "E710", {"start": v(-3.08, -24.02) * mm, "end": v(-4.55, -23.3) * mm});
            skLineSegment(sketch, "E711", {"start": v(-4.55, -23.3) * mm, "end": v(-5.54, -22.59) * mm});
            skLineSegment(sketch, "E712", {"start": v(-5.54, -22.59) * mm, "end": v(-5.84, -22.31) * mm});
            skLineSegment(sketch, "E713", {"start": v(-5.84, -22.31) * mm, "end": v(-6.13, -22.04) * mm});
            skLineSegment(sketch, "E714", {"start": v(-6.13, -22.04) * mm, "end": v(-6.9, -21.11) * mm});
            skLineSegment(sketch, "E715", {"start": v(-6.9, -21.11) * mm, "end": v(-7.67, -19.76) * mm});
            skLineSegment(sketch, "E716", {"start": v(-7.67, -19.76) * mm, "end": v(-8.15, -18.3) * mm});
            skLineSegment(sketch, "E717", {"start": v(-8.15, -18.3) * mm, "end": v(-8.3, -17.14) * mm});
            skLineSegment(sketch, "E718", {"start": v(-8.3, -17.14) * mm, "end": v(-8.3, -16.76) * mm});
            skLineSegment(sketch, "E719", {"start": v(-8.3, -16.76) * mm, "end": v(-8.3, -16.37) * mm});
            skLineSegment(sketch, "E720", {"start": v(-8.3, -16.37) * mm, "end": v(-8.15, -15.22) * mm});
            skLineSegment(sketch, "E721", {"start": v(-8.15, -15.22) * mm, "end": v(-7.67, -13.75) * mm});
            skLineSegment(sketch, "E722", {"start": v(-7.67, -13.75) * mm, "end": v(-6.9, -12.4) * mm});
            skLineSegment(sketch, "E723", {"start": v(-6.9, -12.4) * mm, "end": v(-6.13, -11.47) * mm});
            skLineSegment(sketch, "E724", {"start": v(-6.13, -11.47) * mm, "end": v(-5.84, -11.2) * mm});
            skLineSegment(sketch, "E725", {"start": v(-5.84, -11.2) * mm, "end": v(-5.54, -10.93) * mm});
            skLineSegment(sketch, "E726", {"start": v(-5.54, -10.93) * mm, "end": v(-4.55, -10.22) * mm});
            skLineSegment(sketch, "E727", {"start": v(-4.55, -10.22) * mm, "end": v(-3.08, -9.5) * mm});
            skLineSegment(sketch, "E728", {"start": v(-3.08, -9.5) * mm, "end": v(-1.5, -9.05) * mm});
            skLineSegment(sketch, "E729", {"start": v(-1.5, -9.05) * mm, "end": v(-0.24, -8.9) * mm});
            skLineSegment(sketch, "E730", {"start": v(-0.24, -8.9) * mm, "end": v(0.17, -8.9) * mm});
            skLineSegment(sketch, "E731", {"start": v(0.17, -8.9) * mm, "end": v(0.59, -8.9) * mm});
            skLineSegment(sketch, "E732", {"start": v(0.59, -8.9) * mm, "end": v(1.84, -9.05) * mm});
            skLineSegment(sketch, "E733", {"start": v(1.84, -9.05) * mm, "end": v(3.43, -9.5) * mm});
            skLineSegment(sketch, "E734", {"start": v(3.43, -9.5) * mm, "end": v(4.9, -10.22) * mm});
            skLineSegment(sketch, "E735", {"start": v(4.9, -10.22) * mm, "end": v(5.89, -10.93) * mm});
            skLineSegment(sketch, "E736", {"start": v(5.89, -10.93) * mm, "end": v(6.18, -11.2) * mm});
            skLineSegment(sketch, "E737", {"start": v(6.18, -11.2) * mm, "end": v(6.47, -11.47) * mm});
            skLineSegment(sketch, "E738", {"start": v(6.47, -11.47) * mm, "end": v(7.24, -12.4) * mm});
            skLineSegment(sketch, "E739", {"start": v(7.24, -12.4) * mm, "end": v(8.02, -13.75) * mm});
            skLineSegment(sketch, "E740", {"start": v(8.02, -13.75) * mm, "end": v(8.5, -15.22) * mm});
            skLineSegment(sketch, "E741", {"start": v(8.5, -15.22) * mm, "end": v(8.65, -16.37) * mm});
            skLineSegment(sketch, "E742", {"start": v(8.65, -16.37) * mm, "end": v(8.65, -16.76) * mm});
            skLineSegment(sketch, "E743", {"start": v(-4.73, 5.58) * mm, "end": v(-4.41, 5.37) * mm});
            skLineSegment(sketch, "E744", {"start": v(-4.41, 5.37) * mm, "end": v(-3.55, 4.58) * mm});
            skLineSegment(sketch, "E745", {"start": v(-3.55, 4.58) * mm, "end": v(-2.65, 3.37) * mm});
            skLineSegment(sketch, "E746", {"start": v(-2.65, 3.37) * mm, "end": v(-2.02, 1.97) * mm});
            skLineSegment(sketch, "E747", {"start": v(-2.02, 1.97) * mm, "end": v(-1.68, 0.44) * mm});
            skLineSegment(sketch, "E748", {"start": v(-1.68, 0.44) * mm, "end": v(-1.64, -1.18) * mm});
            skLineSegment(sketch, "E749", {"start": v(-1.64, -1.18) * mm, "end": v(-1.9, -2.84) * mm});
            skLineSegment(sketch, "E750", {"start": v(-1.9, -2.84) * mm, "end": v(-2.45, -4.48) * mm});
            skLineSegment(sketch, "E751", {"start": v(-2.45, -4.48) * mm, "end": v(-3.07, -5.7) * mm});
            skLineSegment(sketch, "E752", {"start": v(-3.07, -5.7) * mm, "end": v(-3.32, -6.08) * mm});
            skLineSegment(sketch, "E753", {"start": v(-3.32, -6.08) * mm, "end": v(-3.57, -6.45) * mm});
            skLineSegment(sketch, "E754", {"start": v(-3.57, -6.45) * mm, "end": v(-4.44, -7.5) * mm});
            skLineSegment(sketch, "E755", {"start": v(-4.44, -7.5) * mm, "end": v(-5.74, -8.66) * mm});
            skLineSegment(sketch, "E756", {"start": v(-5.74, -8.66) * mm, "end": v(-7.17, -9.55) * mm});
            skLineSegment(sketch, "E757", {"start": v(-7.17, -9.55) * mm, "end": v(-8.68, -10.15) * mm});
            skLineSegment(sketch, "E758", {"start": v(-8.68, -10.15) * mm, "end": v(-10.22, -10.45) * mm});
            skLineSegment(sketch, "E759", {"start": v(-10.22, -10.45) * mm, "end": v(-11.76, -10.43) * mm});
            skLineSegment(sketch, "E760", {"start": v(-11.76, -10.43) * mm, "end": v(-13.24, -10.08) * mm});
            skLineSegment(sketch, "E761", {"start": v(-13.24, -10.08) * mm, "end": v(-14.3, -9.6) * mm});
            skLineSegment(sketch, "E762", {"start": v(-14.3, -9.6) * mm, "end": v(-14.63, -9.4) * mm});
            skLineSegment(sketch, "E763", {"start": v(-14.63, -9.4) * mm, "end": v(-14.95, -9.18) * mm});
            skLineSegment(sketch, "E764", {"start": v(-14.95, -9.18) * mm, "end": v(-15.8, -8.4) * mm});
            skLineSegment(sketch, "E765", {"start": v(-15.8, -8.4) * mm, "end": v(-16.71, -7.18) * mm});
            skLineSegment(sketch, "E766", {"start": v(-16.71, -7.18) * mm, "end": v(-17.34, -5.79) * mm});
            skLineSegment(sketch, "E767", {"start": v(-17.34, -5.79) * mm, "end": v(-17.67, -4.26) * mm});
            skLineSegment(sketch, "E768", {"start": v(-17.67, -4.26) * mm, "end": v(-17.72, -2.64) * mm});
            skLineSegment(sketch, "E769", {"start": v(-17.72, -2.64) * mm, "end": v(-17.47, -0.98) * mm});
            skLineSegment(sketch, "E770", {"start": v(-17.47, -0.98) * mm, "end": v(-16.9, 0.66) * mm});
            skLineSegment(sketch, "E771", {"start": v(-16.9, 0.66) * mm, "end": v(-16.29, 1.88) * mm});
            skLineSegment(sketch, "E772", {"start": v(-16.29, 1.88) * mm, "end": v(-16.04, 2.26) * mm});
            skLineSegment(sketch, "E773", {"start": v(-16.04, 2.26) * mm, "end": v(-15.8, 2.64) * mm});
            skLineSegment(sketch, "E774", {"start": v(-15.8, 2.64) * mm, "end": v(-14.91, 3.68) * mm});
            skLineSegment(sketch, "E775", {"start": v(-14.91, 3.68) * mm, "end": v(-13.61, 4.84) * mm});
            skLineSegment(sketch, "E776", {"start": v(-13.61, 4.84) * mm, "end": v(-12.19, 5.73) * mm});
            skLineSegment(sketch, "E777", {"start": v(-12.19, 5.73) * mm, "end": v(-10.68, 6.33) * mm});
            skLineSegment(sketch, "E778", {"start": v(-10.68, 6.33) * mm, "end": v(-9.13, 6.63) * mm});
            skLineSegment(sketch, "E779", {"start": v(-9.13, 6.63) * mm, "end": v(-7.6, 6.6) * mm});
            skLineSegment(sketch, "E780", {"start": v(-7.6, 6.6) * mm, "end": v(-6.12, 6.26) * mm});
            skLineSegment(sketch, "E781", {"start": v(-6.12, 6.26) * mm, "end": v(-5.05, 5.79) * mm});
            skLineSegment(sketch, "E782", {"start": v(-5.05, 5.79) * mm, "end": v(-4.73, 5.58) * mm});
            skLineSegment(sketch, "E783", {"start": v(4.75, 6) * mm, "end": v(4.43, 5.78) * mm});
            skLineSegment(sketch, "E784", {"start": v(4.43, 5.78) * mm, "end": v(3.57, 5) * mm});
            skLineSegment(sketch, "E785", {"start": v(3.57, 5) * mm, "end": v(2.66, 3.78) * mm});
            skLineSegment(sketch, "E786", {"start": v(2.66, 3.78) * mm, "end": v(2.04, 2.38) * mm});
            skLineSegment(sketch, "E787", {"start": v(2.04, 2.38) * mm, "end": v(1.7, 0.85) * mm});
            skLineSegment(sketch, "E788", {"start": v(1.7, 0.85) * mm, "end": v(1.65, -0.76) * mm});
            skLineSegment(sketch, "E789", {"start": v(1.65, -0.76) * mm, "end": v(1.9, -2.42) * mm});
            skLineSegment(sketch, "E790", {"start": v(1.9, -2.42) * mm, "end": v(2.47, -4.07) * mm});
            skLineSegment(sketch, "E791", {"start": v(2.47, -4.07) * mm, "end": v(3.08, -5.28) * mm});
            skLineSegment(sketch, "E792", {"start": v(3.08, -5.28) * mm, "end": v(3.33, -5.66) * mm});
            skLineSegment(sketch, "E793", {"start": v(3.33, -5.66) * mm, "end": v(3.58, -6.04) * mm});
            skLineSegment(sketch, "E794", {"start": v(3.58, -6.04) * mm, "end": v(4.46, -7.08) * mm});
            skLineSegment(sketch, "E795", {"start": v(4.46, -7.08) * mm, "end": v(5.76, -8.25) * mm});
            skLineSegment(sketch, "E796", {"start": v(5.76, -8.25) * mm, "end": v(7.19, -9.13) * mm});
            skLineSegment(sketch, "E797", {"start": v(7.19, -9.13) * mm, "end": v(8.7, -9.73) * mm});
            skLineSegment(sketch, "E798", {"start": v(8.7, -9.73) * mm, "end": v(10.24, -10.03) * mm});
            skLineSegment(sketch, "E799", {"start": v(10.24, -10.03) * mm, "end": v(11.78, -10.01) * mm});
            skLineSegment(sketch, "E800", {"start": v(11.78, -10.01) * mm, "end": v(13.26, -9.67) * mm});
            skLineSegment(sketch, "E801", {"start": v(13.26, -9.67) * mm, "end": v(14.32, -9.19) * mm});
            skLineSegment(sketch, "E802", {"start": v(14.32, -9.19) * mm, "end": v(14.64, -8.98) * mm});
            skLineSegment(sketch, "E803", {"start": v(14.64, -8.98) * mm, "end": v(14.96, -8.77) * mm});
            skLineSegment(sketch, "E804", {"start": v(14.96, -8.77) * mm, "end": v(15.82, -7.99) * mm});
            skLineSegment(sketch, "E805", {"start": v(15.82, -7.99) * mm, "end": v(16.73, -6.77) * mm});
            skLineSegment(sketch, "E806", {"start": v(16.73, -6.77) * mm, "end": v(17.35, -5.37) * mm});
            skLineSegment(sketch, "E807", {"start": v(17.35, -5.37) * mm, "end": v(17.7, -3.84) * mm});
            skLineSegment(sketch, "E808", {"start": v(17.7, -3.84) * mm, "end": v(17.73, -2.22) * mm});
            skLineSegment(sketch, "E809", {"start": v(17.73, -2.22) * mm, "end": v(17.48, -0.57) * mm});
            skLineSegment(sketch, "E810", {"start": v(17.48, -0.57) * mm, "end": v(16.92, 1.08) * mm});
            skLineSegment(sketch, "E811", {"start": v(16.92, 1.08) * mm, "end": v(16.3, 2.3) * mm});
            skLineSegment(sketch, "E812", {"start": v(16.3, 2.3) * mm, "end": v(16.06, 2.67) * mm});
            skLineSegment(sketch, "E813", {"start": v(16.06, 2.67) * mm, "end": v(15.8, 3.05) * mm});
            skLineSegment(sketch, "E814", {"start": v(15.8, 3.05) * mm, "end": v(14.93, 4.1) * mm});
            skLineSegment(sketch, "E815", {"start": v(14.93, 4.1) * mm, "end": v(13.63, 5.26) * mm});
            skLineSegment(sketch, "E816", {"start": v(13.63, 5.26) * mm, "end": v(12.2, 6.15) * mm});
            skLineSegment(sketch, "E817", {"start": v(12.2, 6.15) * mm, "end": v(10.7, 6.75) * mm});
            skLineSegment(sketch, "E818", {"start": v(10.7, 6.75) * mm, "end": v(9.15, 7.04) * mm});
            skLineSegment(sketch, "E819", {"start": v(9.15, 7.04) * mm, "end": v(7.61, 7.03) * mm});
            skLineSegment(sketch, "E820", {"start": v(7.61, 7.03) * mm, "end": v(6.13, 6.68) * mm});
            skLineSegment(sketch, "E821", {"start": v(6.13, 6.68) * mm, "end": v(5.07, 6.2) * mm});
            skLineSegment(sketch, "E822", {"start": v(5.07, 6.2) * mm, "end": v(4.75, 6) * mm});
            skLineSegment(sketch, "E823", {"start": v(-22.29, 1.81) * mm, "end": v(-22.14, 1.85) * mm});
            skLineSegment(sketch, "E824", {"start": v(-22.14, 1.85) * mm, "end": v(-21.65, 1.8) * mm});
            skLineSegment(sketch, "E825", {"start": v(-21.65, 1.8) * mm, "end": v(-21.15, 1.43) * mm});
            skLineSegment(sketch, "E826", {"start": v(-21.15, 1.43) * mm, "end": v(-20.78, 0.75) * mm});
            skLineSegment(sketch, "E827", {"start": v(-20.78, 0.75) * mm, "end": v(-20.54, -0.19) * mm});
            skLineSegment(sketch, "E828", {"start": v(-20.54, -0.19) * mm, "end": v(-20.4, -1.33) * mm});
            skLineSegment(sketch, "E829", {"start": v(-20.4, -1.33) * mm, "end": v(-20.38, -2.63) * mm});
            skLineSegment(sketch, "E830", {"start": v(-20.38, -2.63) * mm, "end": v(-20.45, -4.03) * mm});
            skLineSegment(sketch, "E831", {"start": v(-20.45, -4.03) * mm, "end": v(-20.61, -5.48) * mm});
            skLineSegment(sketch, "E832", {"start": v(-20.61, -5.48) * mm, "end": v(-20.85, -6.92) * mm});
            skLineSegment(sketch, "E833", {"start": v(-20.85, -6.92) * mm, "end": v(-21.17, -8.31) * mm});
            skLineSegment(sketch, "E834", {"start": v(-21.17, -8.31) * mm, "end": v(-21.55, -9.59) * mm});
            skLineSegment(sketch, "E835", {"start": v(-21.55, -9.59) * mm, "end": v(-21.98, -10.7) * mm});
            skLineSegment(sketch, "E836", {"start": v(-21.98, -10.7) * mm, "end": v(-22.46, -11.6) * mm});
            skLineSegment(sketch, "E837", {"start": v(-22.46, -11.6) * mm, "end": v(-22.98, -12.24) * mm});
            skLineSegment(sketch, "E838", {"start": v(-22.98, -12.24) * mm, "end": v(-23.53, -12.56) * mm});
            skLineSegment(sketch, "E839", {"start": v(-23.53, -12.56) * mm, "end": v(-23.97, -12.56) * mm});
            skLineSegment(sketch, "E840", {"start": v(-23.97, -12.56) * mm, "end": v(-24.1, -12.5) * mm});
            skLineSegment(sketch, "E841", {"start": v(-24.1, -12.5) * mm, "end": v(-24.26, -12.38) * mm});
            skLineSegment(sketch, "E842", {"start": v(-24.26, -12.38) * mm, "end": v(-24.7, -11.94) * mm});
            skLineSegment(sketch, "E843", {"start": v(-24.7, -11.94) * mm, "end": v(-25.25, -11.26) * mm});
            skLineSegment(sketch, "E844", {"start": v(-25.25, -11.26) * mm, "end": v(-25.73, -10.48) * mm});
            skLineSegment(sketch, "E845", {"start": v(-25.73, -10.48) * mm, "end": v(-26.13, -9.62) * mm});
            skLineSegment(sketch, "E846", {"start": v(-26.13, -9.62) * mm, "end": v(-26.45, -8.7) * mm});
            skLineSegment(sketch, "E847", {"start": v(-26.45, -8.7) * mm, "end": v(-26.68, -7.72) * mm});
            skLineSegment(sketch, "E848", {"start": v(-26.68, -7.72) * mm, "end": v(-26.8, -6.7) * mm});
            skLineSegment(sketch, "E849", {"start": v(-26.8, -6.7) * mm, "end": v(-26.83, -5.67) * mm});
            skLineSegment(sketch, "E850", {"start": v(-26.83, -5.67) * mm, "end": v(-26.73, -4.62) * mm});
            skLineSegment(sketch, "E851", {"start": v(-26.73, -4.62) * mm, "end": v(-26.52, -3.58) * mm});
            skLineSegment(sketch, "E852", {"start": v(-26.52, -3.58) * mm, "end": v(-26.18, -2.55) * mm});
            skLineSegment(sketch, "E853", {"start": v(-26.18, -2.55) * mm, "end": v(-25.7, -1.56) * mm});
            skLineSegment(sketch, "E854", {"start": v(-25.7, -1.56) * mm, "end": v(-25.08, -0.6) * mm});
            skLineSegment(sketch, "E855", {"start": v(-25.08, -0.6) * mm, "end": v(-24.31, 0.28) * mm});
            skLineSegment(sketch, "E856", {"start": v(-24.31, 0.28) * mm, "end": v(-23.38, 1.09) * mm});
            skLineSegment(sketch, "E857", {"start": v(-23.38, 1.09) * mm, "end": v(-22.57, 1.65) * mm});
            skLineSegment(sketch, "E858", {"start": v(-22.57, 1.65) * mm, "end": v(-22.29, 1.81) * mm});
            skLineSegment(sketch, "E859", {"start": v(21.54, 2.02) * mm, "end": v(21.4, 2.06) * mm});
            skLineSegment(sketch, "E860", {"start": v(21.4, 2.06) * mm, "end": v(20.9, 2.01) * mm});
            skLineSegment(sketch, "E861", {"start": v(20.9, 2.01) * mm, "end": v(20.4, 1.64) * mm});
            skLineSegment(sketch, "E862", {"start": v(20.4, 1.64) * mm, "end": v(20.03, 0.96) * mm});
            skLineSegment(sketch, "E863", {"start": v(20.03, 0.96) * mm, "end": v(19.79, 0.02) * mm});
            skLineSegment(sketch, "E864", {"start": v(19.79, 0.02) * mm, "end": v(19.66, -1.13) * mm});
            skLineSegment(sketch, "E865", {"start": v(19.66, -1.13) * mm, "end": v(19.63, -2.43) * mm});
            skLineSegment(sketch, "E866", {"start": v(19.63, -2.43) * mm, "end": v(19.7, -3.82) * mm});
            skLineSegment(sketch, "E867", {"start": v(19.7, -3.82) * mm, "end": v(19.86, -5.27) * mm});
            skLineSegment(sketch, "E868", {"start": v(19.86, -5.27) * mm, "end": v(20.1, -6.72) * mm});
            skLineSegment(sketch, "E869", {"start": v(20.1, -6.72) * mm, "end": v(20.42, -8.1) * mm});
            skLineSegment(sketch, "E870", {"start": v(20.42, -8.1) * mm, "end": v(20.8, -9.38) * mm});
            skLineSegment(sketch, "E871", {"start": v(20.8, -9.38) * mm, "end": v(21.23, -10.5) * mm});
            skLineSegment(sketch, "E872", {"start": v(21.23, -10.5) * mm, "end": v(21.7, -11.4) * mm});
            skLineSegment(sketch, "E873", {"start": v(21.7, -11.4) * mm, "end": v(22.23, -12.04) * mm});
            skLineSegment(sketch, "E874", {"start": v(22.23, -12.04) * mm, "end": v(22.77, -12.35) * mm});
            skLineSegment(sketch, "E875", {"start": v(22.77, -12.35) * mm, "end": v(23.22, -12.35) * mm});
            skLineSegment(sketch, "E876", {"start": v(23.22, -12.35) * mm, "end": v(23.35, -12.3) * mm});
            skLineSegment(sketch, "E877", {"start": v(23.35, -12.3) * mm, "end": v(23.5, -12.17) * mm});
            skLineSegment(sketch, "E878", {"start": v(23.5, -12.17) * mm, "end": v(23.95, -11.73) * mm});
            skLineSegment(sketch, "E879", {"start": v(23.95, -11.73) * mm, "end": v(24.5, -11.05) * mm});
            skLineSegment(sketch, "E880", {"start": v(24.5, -11.05) * mm, "end": v(24.98, -10.27) * mm});
            skLineSegment(sketch, "E881", {"start": v(24.98, -10.27) * mm, "end": v(25.38, -9.42) * mm});
            skLineSegment(sketch, "E882", {"start": v(25.38, -9.42) * mm, "end": v(25.7, -8.5) * mm});
            skLineSegment(sketch, "E883", {"start": v(25.7, -8.5) * mm, "end": v(25.93, -7.52) * mm});
            skLineSegment(sketch, "E884", {"start": v(25.93, -7.52) * mm, "end": v(26.05, -6.5) * mm});
            skLineSegment(sketch, "E885", {"start": v(26.05, -6.5) * mm, "end": v(26.08, -5.46) * mm});
            skLineSegment(sketch, "E886", {"start": v(26.08, -5.46) * mm, "end": v(25.98, -4.41) * mm});
            skLineSegment(sketch, "E887", {"start": v(25.98, -4.41) * mm, "end": v(25.77, -3.37) * mm});
            skLineSegment(sketch, "E888", {"start": v(25.77, -3.37) * mm, "end": v(25.43, -2.34) * mm});
            skLineSegment(sketch, "E889", {"start": v(25.43, -2.34) * mm, "end": v(24.95, -1.35) * mm});
            skLineSegment(sketch, "E890", {"start": v(24.95, -1.35) * mm, "end": v(24.33, -0.4) * mm});
            skLineSegment(sketch, "E891", {"start": v(24.33, -0.4) * mm, "end": v(23.56, 0.49) * mm});
            skLineSegment(sketch, "E892", {"start": v(23.56, 0.49) * mm, "end": v(22.63, 1.3) * mm});
            skLineSegment(sketch, "E893", {"start": v(22.63, 1.3) * mm, "end": v(21.82, 1.86) * mm});
            skLineSegment(sketch, "E894", {"start": v(21.82, 1.86) * mm, "end": v(21.54, 2.02) * mm});
            skLineSegment(sketch, "E895", {"start": v(8.65, 14.46) * mm, "end": v(9.24, 14.56) * mm});
            skLineSegment(sketch, "E896", {"start": v(9.24, 14.56) * mm, "end": v(11.05, 14.65) * mm});
            skLineSegment(sketch, "E897", {"start": v(11.05, 14.65) * mm, "end": v(13.29, 14.38) * mm});
            skLineSegment(sketch, "E898", {"start": v(13.29, 14.38) * mm, "end": v(15.31, 13.7) * mm});
            skLineSegment(sketch, "E899", {"start": v(15.31, 13.7) * mm, "end": v(17.08, 12.6) * mm});
            skLineSegment(sketch, "E900", {"start": v(17.08, 12.6) * mm, "end": v(18.52, 11.12) * mm});
            skLineSegment(sketch, "E901", {"start": v(18.52, 11.12) * mm, "end": v(19.6, 9.28) * mm});
            skLineSegment(sketch, "E902", {"start": v(19.6, 9.28) * mm, "end": v(20.25, 7.09) * mm});
            skLineSegment(sketch, "E903", {"start": v(20.25, 7.09) * mm, "end": v(20.44, 5.2) * mm});
            skLineSegment(sketch, "E904", {"start": v(20.44, 5.2) * mm, "end": v(20.43, 4.58) * mm});
            skLineSegment(sketch, "E905", {"start": v(20.43, 4.58) * mm, "end": v(20.42, 4.5) * mm});
            skLineSegment(sketch, "E906", {"start": v(20.42, 4.5) * mm, "end": v(20.23, 4.24) * mm});
            skLineSegment(sketch, "E907", {"start": v(20.23, 4.24) * mm, "end": v(19.76, 4.2) * mm});
            skLineSegment(sketch, "E908", {"start": v(19.76, 4.2) * mm, "end": v(19.05, 4.45) * mm});
            skLineSegment(sketch, "E909", {"start": v(19.05, 4.45) * mm, "end": v(18.16, 4.92) * mm});
            skLineSegment(sketch, "E910", {"start": v(18.16, 4.92) * mm, "end": v(17.11, 5.59) * mm});
            skLineSegment(sketch, "E911", {"start": v(17.11, 5.59) * mm, "end": v(15.97, 6.4) * mm});
            skLineSegment(sketch, "E912", {"start": v(15.97, 6.4) * mm, "end": v(14.77, 7.34) * mm});
            skLineSegment(sketch, "E913", {"start": v(14.77, 7.34) * mm, "end": v(13.55, 8.35) * mm});
            skLineSegment(sketch, "E914", {"start": v(13.55, 8.35) * mm, "end": v(12.37, 9.4) * mm});
            skLineSegment(sketch, "E915", {"start": v(12.37, 9.4) * mm, "end": v(11.26, 10.44) * mm});
            skLineSegment(sketch, "E916", {"start": v(11.26, 10.44) * mm, "end": v(10.27, 11.44) * mm});
            skLineSegment(sketch, "E917", {"start": v(10.27, 11.44) * mm, "end": v(9.45, 12.37) * mm});
            skLineSegment(sketch, "E918", {"start": v(9.45, 12.37) * mm, "end": v(8.83, 13.17) * mm});
            skLineSegment(sketch, "E919", {"start": v(8.83, 13.17) * mm, "end": v(8.46, 13.81) * mm});
            skLineSegment(sketch, "E920", {"start": v(8.46, 13.81) * mm, "end": v(8.39, 14.26) * mm});
            skLineSegment(sketch, "E921", {"start": v(8.39, 14.26) * mm, "end": v(8.58, 14.45) * mm});
            skLineSegment(sketch, "E922", {"start": v(8.58, 14.45) * mm, "end": v(8.65, 14.46) * mm});
            skLineSegment(sketch, "E923", {"start": v(-9.43, 14.67) * mm, "end": v(-10.02, 14.77) * mm});
            skLineSegment(sketch, "E924", {"start": v(-10.02, 14.77) * mm, "end": v(-11.82, 14.85) * mm});
            skLineSegment(sketch, "E925", {"start": v(-11.82, 14.85) * mm, "end": v(-14.06, 14.6) * mm});
            skLineSegment(sketch, "E926", {"start": v(-14.06, 14.6) * mm, "end": v(-16.1, 13.9) * mm});
            skLineSegment(sketch, "E927", {"start": v(-16.1, 13.9) * mm, "end": v(-17.85, 12.8) * mm});
            skLineSegment(sketch, "E928", {"start": v(-17.85, 12.8) * mm, "end": v(-19.3, 11.33) * mm});
            skLineSegment(sketch, "E929", {"start": v(-19.3, 11.33) * mm, "end": v(-20.38, 9.48) * mm});
            skLineSegment(sketch, "E930", {"start": v(-20.38, 9.48) * mm, "end": v(-21.03, 7.3) * mm});
            skLineSegment(sketch, "E931", {"start": v(-21.03, 7.3) * mm, "end": v(-21.22, 5.41) * mm});
            skLineSegment(sketch, "E932", {"start": v(-21.22, 5.41) * mm, "end": v(-21.2, 4.79) * mm});
            skLineSegment(sketch, "E933", {"start": v(-21.2, 4.79) * mm, "end": v(-21.2, 4.7) * mm});
            skLineSegment(sketch, "E934", {"start": v(-21.2, 4.7) * mm, "end": v(-21, 4.45) * mm});
            skLineSegment(sketch, "E935", {"start": v(-21, 4.45) * mm, "end": v(-20.54, 4.42) * mm});
            skLineSegment(sketch, "E936", {"start": v(-20.54, 4.42) * mm, "end": v(-19.83, 4.66) * mm});
            skLineSegment(sketch, "E937", {"start": v(-19.83, 4.66) * mm, "end": v(-18.93, 5.13) * mm});
            skLineSegment(sketch, "E938", {"start": v(-18.93, 5.13) * mm, "end": v(-17.9, 5.8) * mm});
            skLineSegment(sketch, "E939", {"start": v(-17.9, 5.8) * mm, "end": v(-16.75, 6.61) * mm});
            skLineSegment(sketch, "E940", {"start": v(-16.75, 6.61) * mm, "end": v(-15.55, 7.55) * mm});
            skLineSegment(sketch, "E941", {"start": v(-15.55, 7.55) * mm, "end": v(-14.33, 8.56) * mm});
            skLineSegment(sketch, "E942", {"start": v(-14.33, 8.56) * mm, "end": v(-13.15, 9.6) * mm});
            skLineSegment(sketch, "E943", {"start": v(-13.15, 9.6) * mm, "end": v(-12.04, 10.65) * mm});
            skLineSegment(sketch, "E944", {"start": v(-12.04, 10.65) * mm, "end": v(-11.05, 11.65) * mm});
            skLineSegment(sketch, "E945", {"start": v(-11.05, 11.65) * mm, "end": v(-10.22, 12.57) * mm});
            skLineSegment(sketch, "E946", {"start": v(-10.22, 12.57) * mm, "end": v(-9.6, 13.38) * mm});
            skLineSegment(sketch, "E947", {"start": v(-9.6, 13.38) * mm, "end": v(-9.24, 14.02) * mm});
            skLineSegment(sketch, "E948", {"start": v(-9.24, 14.02) * mm, "end": v(-9.16, 14.46) * mm});
            skLineSegment(sketch, "E949", {"start": v(-9.16, 14.46) * mm, "end": v(-9.36, 14.66) * mm});
            skLineSegment(sketch, "E950", {"start": v(-9.36, 14.66) * mm, "end": v(-9.43, 14.67) * mm});
            skLineSegment(sketch, "E951", {"start": v(-0.03, 16.33) * mm, "end": v(-0.4, 16.34) * mm});
            skLineSegment(sketch, "E952", {"start": v(-0.4, 16.34) * mm, "end": v(-1.48, 16.23) * mm});
            skLineSegment(sketch, "E953", {"start": v(-1.48, 16.23) * mm, "end": v(-2.87, 15.89) * mm});
            skLineSegment(sketch, "E954", {"start": v(-2.87, 15.89) * mm, "end": v(-4.17, 15.36) * mm});
            skLineSegment(sketch, "E955", {"start": v(-4.17, 15.36) * mm, "end": v(-5.32, 14.7) * mm});
            skLineSegment(sketch, "E956", {"start": v(-5.32, 14.7) * mm, "end": v(-6.3, 13.95) * mm});
            skLineSegment(sketch, "E957", {"start": v(-6.3, 13.95) * mm, "end": v(-7.04, 13.16) * mm});
            skLineSegment(sketch, "E958", {"start": v(-7.04, 13.16) * mm, "end": v(-7.52, 12.39) * mm});
            skLineSegment(sketch, "E959", {"start": v(-7.52, 12.39) * mm, "end": v(-7.7, 11.86) * mm});
            skLineSegment(sketch, "E960", {"start": v(-7.7, 11.86) * mm, "end": v(-7.7, 11.69) * mm});
            skLineSegment(sketch, "E961", {"start": v(-7.7, 11.69) * mm, "end": v(-7.7, 11.49) * mm});
            skLineSegment(sketch, "E962", {"start": v(-7.7, 11.49) * mm, "end": v(-7.56, 10.9) * mm});
            skLineSegment(sketch, "E963", {"start": v(-7.56, 10.9) * mm, "end": v(-7.14, 10.12) * mm});
            skLineSegment(sketch, "E964", {"start": v(-7.14, 10.12) * mm, "end": v(-6.48, 9.4) * mm});
            skLineSegment(sketch, "E965", {"start": v(-6.48, 9.4) * mm, "end": v(-5.58, 8.75) * mm});
            skLineSegment(sketch, "E966", {"start": v(-5.58, 8.75) * mm, "end": v(-4.46, 8.19) * mm});
            skLineSegment(sketch, "E967", {"start": v(-4.46, 8.19) * mm, "end": v(-3.15, 7.75) * mm});
            skLineSegment(sketch, "E968", {"start": v(-3.15, 7.75) * mm, "end": v(-1.65, 7.47) * mm});
            skLineSegment(sketch, "E969", {"start": v(-1.65, 7.47) * mm, "end": v(-0.42, 7.36) * mm});
            skLineSegment(sketch, "E970", {"start": v(-0.42, 7.36) * mm, "end": v(0, 7.35) * mm});
            skLineSegment(sketch, "E971", {"start": v(0, 7.35) * mm, "end": v(0.42, 7.35) * mm});
            skLineSegment(sketch, "E972", {"start": v(0.42, 7.35) * mm, "end": v(1.68, 7.42) * mm});
            skLineSegment(sketch, "E973", {"start": v(1.68, 7.42) * mm, "end": v(3.18, 7.64) * mm});
            skLineSegment(sketch, "E974", {"start": v(3.18, 7.64) * mm, "end": v(4.5, 8) * mm});
            skLineSegment(sketch, "E975", {"start": v(4.5, 8) * mm, "end": v(5.61, 8.48) * mm});
            skLineSegment(sketch, "E976", {"start": v(5.61, 8.48) * mm, "end": v(6.5, 9.06) * mm});
            skLineSegment(sketch, "E977", {"start": v(6.5, 9.06) * mm, "end": v(7.16, 9.73) * mm});
            skLineSegment(sketch, "E978", {"start": v(7.16, 9.73) * mm, "end": v(7.57, 10.47) * mm});
            skLineSegment(sketch, "E979", {"start": v(7.57, 10.47) * mm, "end": v(7.71, 11.07) * mm});
            skLineSegment(sketch, "E980", {"start": v(7.71, 11.07) * mm, "end": v(7.71, 11.27) * mm});
            skLineSegment(sketch, "E981", {"start": v(7.71, 11.27) * mm, "end": v(7.71, 11.5) * mm});
            skLineSegment(sketch, "E982", {"start": v(7.71, 11.5) * mm, "end": v(7.53, 12.2) * mm});
            skLineSegment(sketch, "E983", {"start": v(7.53, 12.2) * mm, "end": v(7, 13.1) * mm});
            skLineSegment(sketch, "E984", {"start": v(7, 13.1) * mm, "end": v(6.18, 13.96) * mm});
            skLineSegment(sketch, "E985", {"start": v(6.18, 13.96) * mm, "end": v(5.15, 14.74) * mm});
            skLineSegment(sketch, "E986", {"start": v(5.15, 14.74) * mm, "end": v(3.95, 15.4) * mm});
            skLineSegment(sketch, "E987", {"start": v(3.95, 15.4) * mm, "end": v(2.65, 15.9) * mm});
            skLineSegment(sketch, "E988", {"start": v(2.65, 15.9) * mm, "end": v(1.3, 16.22) * mm});
            skLineSegment(sketch, "E989", {"start": v(1.3, 16.22) * mm, "end": v(0.3, 16.33) * mm});
            skLineSegment(sketch, "E990", {"start": v(0.3, 16.33) * mm, "end": v(-0.03, 16.33) * mm});
            skLineSegment(sketch, "E991", {"start": v(0.21, -27.04) * mm, "end": v(0.54, -27.03) * mm});
            skLineSegment(sketch, "E992", {"start": v(0.54, -27.03) * mm, "end": v(1.53, -27.05) * mm});
            skLineSegment(sketch, "E993", {"start": v(1.53, -27.05) * mm, "end": v(2.9, -27.18) * mm});
            skLineSegment(sketch, "E994", {"start": v(2.9, -27.18) * mm, "end": v(4.23, -27.41) * mm});
            skLineSegment(sketch, "E995", {"start": v(4.23, -27.41) * mm, "end": v(5.48, -27.74) * mm});
            skLineSegment(sketch, "E996", {"start": v(5.48, -27.74) * mm, "end": v(6.56, -28.16) * mm});
            skLineSegment(sketch, "E997", {"start": v(6.56, -28.16) * mm, "end": v(7.42, -28.65) * mm});
            skLineSegment(sketch, "E998", {"start": v(7.42, -28.65) * mm, "end": v(7.99, -29.2) * mm});
            skLineSegment(sketch, "E999", {"start": v(7.99, -29.2) * mm, "end": v(8.2, -29.64) * mm});
            skLineSegment(sketch, "E1000", {"start": v(8.2, -29.64) * mm, "end": v(8.2, -29.8) * mm});
            skLineSegment(sketch, "E1001", {"start": v(8.2, -29.8) * mm, "end": v(8.2, -29.96) * mm});
            skLineSegment(sketch, "E1002", {"start": v(8.2, -29.96) * mm, "end": v(8.02, -30.48) * mm});
            skLineSegment(sketch, "E1003", {"start": v(8.02, -30.48) * mm, "end": v(7.5, -31.29) * mm});
            skLineSegment(sketch, "E1004", {"start": v(7.5, -31.29) * mm, "end": v(6.7, -32.15) * mm});
            skLineSegment(sketch, "E1005", {"start": v(6.7, -32.15) * mm, "end": v(5.64, -33) * mm});
            skLineSegment(sketch, "E1006", {"start": v(5.64, -33) * mm, "end": v(4.38, -33.78) * mm});
            skLineSegment(sketch, "E1007", {"start": v(4.38, -33.78) * mm, "end": v(3, -34.4) * mm});
            skLineSegment(sketch, "E1008", {"start": v(3, -34.4) * mm, "end": v(1.5, -34.82) * mm});
            skLineSegment(sketch, "E1009", {"start": v(1.5, -34.82) * mm, "end": v(0.36, -34.96) * mm});
            skLineSegment(sketch, "E1010", {"start": v(0.36, -34.96) * mm, "end": v(-0.02, -34.95) * mm});
            skLineSegment(sketch, "E1011", {"start": v(-0.02, -34.95) * mm, "end": v(-0.4, -34.97) * mm});
            skLineSegment(sketch, "E1012", {"start": v(-0.4, -34.97) * mm, "end": v(-1.58, -34.86) * mm});
            skLineSegment(sketch, "E1013", {"start": v(-1.58, -34.86) * mm, "end": v(-3.1, -34.47) * mm});
            skLineSegment(sketch, "E1014", {"start": v(-3.1, -34.47) * mm, "end": v(-4.5, -33.88) * mm});
            skLineSegment(sketch, "E1015", {"start": v(-4.5, -33.88) * mm, "end": v(-5.76, -33.14) * mm});
            skLineSegment(sketch, "E1016", {"start": v(-5.76, -33.14) * mm, "end": v(-6.82, -32.34) * mm});
            skLineSegment(sketch, "E1017", {"start": v(-6.82, -32.34) * mm, "end": v(-7.62, -31.54) * mm});
            skLineSegment(sketch, "E1018", {"start": v(-7.62, -31.54) * mm, "end": v(-8.13, -30.82) * mm});
            skLineSegment(sketch, "E1019", {"start": v(-8.13, -30.82) * mm, "end": v(-8.3, -30.39) * mm});
            skLineSegment(sketch, "E1020", {"start": v(-8.3, -30.39) * mm, "end": v(-8.3, -30.25) * mm});
            skLineSegment(sketch, "E1021", {"start": v(-8.3, -30.25) * mm, "end": v(-8.3, -30.08) * mm});
            skLineSegment(sketch, "E1022", {"start": v(-8.3, -30.08) * mm, "end": v(-8.1, -29.58) * mm});
            skLineSegment(sketch, "E1023", {"start": v(-8.1, -29.58) * mm, "end": v(-7.47, -28.96) * mm});
            skLineSegment(sketch, "E1024", {"start": v(-7.47, -28.96) * mm, "end": v(-6.53, -28.4) * mm});
            skLineSegment(sketch, "E1025", {"start": v(-6.53, -28.4) * mm, "end": v(-5.34, -27.92) * mm});
            skLineSegment(sketch, "E1026", {"start": v(-5.34, -27.92) * mm, "end": v(-3.99, -27.53) * mm});
            skLineSegment(sketch, "E1027", {"start": v(-3.99, -27.53) * mm, "end": v(-2.56, -27.25) * mm});
            skLineSegment(sketch, "E1028", {"start": v(-2.56, -27.25) * mm, "end": v(-1.13, -27.08) * mm});
            skLineSegment(sketch, "E1029", {"start": v(-1.13, -27.08) * mm, "end": v(-0.12, -27.04) * mm});
            skLineSegment(sketch, "E1030", {"start": v(-0.12, -27.04) * mm, "end": v(0.21, -27.04) * mm});
            skLineSegment(sketch, "E1031", {"start": v(-12.37, -17.25) * mm, "end": v(-12.14, -17.53) * mm});
            skLineSegment(sketch, "E1032", {"start": v(-12.14, -17.53) * mm, "end": v(-11.53, -18.44) * mm});
            skLineSegment(sketch, "E1033", {"start": v(-11.53, -18.44) * mm, "end": v(-10.83, -19.77) * mm});
            skLineSegment(sketch, "E1034", {"start": v(-10.83, -19.77) * mm, "end": v(-10.3, -21.16) * mm});
            skLineSegment(sketch, "E1035", {"start": v(-10.3, -21.16) * mm, "end": v(-9.95, -22.56) * mm});
            skLineSegment(sketch, "E1036", {"start": v(-9.95, -22.56) * mm, "end": v(-9.81, -23.9) * mm});
            skLineSegment(sketch, "E1037", {"start": v(-9.81, -23.9) * mm, "end": v(-9.9, -25.1) * mm});
            skLineSegment(sketch, "E1038", {"start": v(-9.9, -25.1) * mm, "end": v(-10.25, -26.1) * mm});
            skLineSegment(sketch, "E1039", {"start": v(-10.25, -26.1) * mm, "end": v(-10.68, -26.68) * mm});
            skLineSegment(sketch, "E1040", {"start": v(-10.68, -26.68) * mm, "end": v(-10.86, -26.82) * mm});
            skLineSegment(sketch, "E1041", {"start": v(-10.86, -26.82) * mm, "end": v(-11.06, -26.93) * mm});
            skLineSegment(sketch, "E1042", {"start": v(-11.06, -26.93) * mm, "end": v(-11.7, -27.17) * mm});
            skLineSegment(sketch, "E1043", {"start": v(-11.7, -27.17) * mm, "end": v(-12.75, -27.34) * mm});
            skLineSegment(sketch, "E1044", {"start": v(-12.75, -27.34) * mm, "end": v(-13.96, -27.3) * mm});
            skLineSegment(sketch, "E1045", {"start": v(-13.96, -27.3) * mm, "end": v(-15.28, -27) * mm});
            skLineSegment(sketch, "E1046", {"start": v(-15.28, -27) * mm, "end": v(-16.66, -26.43) * mm});
            skLineSegment(sketch, "E1047", {"start": v(-16.66, -26.43) * mm, "end": v(-18.07, -25.55) * mm});
            skLineSegment(sketch, "E1048", {"start": v(-18.07, -25.55) * mm, "end": v(-19.44, -24.33) * mm});
            skLineSegment(sketch, "E1049", {"start": v(-19.44, -24.33) * mm, "end": v(-20.44, -23.17) * mm});
            skLineSegment(sketch, "E1050", {"start": v(-20.44, -23.17) * mm, "end": v(-20.73, -22.75) * mm});
            skLineSegment(sketch, "E1051", {"start": v(-20.73, -22.75) * mm, "end": v(-20.93, -22.39) * mm});
            skLineSegment(sketch, "E1052", {"start": v(-20.93, -22.39) * mm, "end": v(-21.45, -21.26) * mm});
            skLineSegment(sketch, "E1053", {"start": v(-21.45, -21.26) * mm, "end": v(-21.95, -19.8) * mm});
            skLineSegment(sketch, "E1054", {"start": v(-21.95, -19.8) * mm, "end": v(-22.24, -18.4) * mm});
            skLineSegment(sketch, "E1055", {"start": v(-22.24, -18.4) * mm, "end": v(-22.34, -17.09) * mm});
            skLineSegment(sketch, "E1056", {"start": v(-22.34, -17.09) * mm, "end": v(-22.26, -15.91) * mm});
            skLineSegment(sketch, "E1057", {"start": v(-22.26, -15.91) * mm, "end": v(-22.02, -14.9) * mm});
            skLineSegment(sketch, "E1058", {"start": v(-22.02, -14.9) * mm, "end": v(-21.63, -14.1) * mm});
            skLineSegment(sketch, "E1059", {"start": v(-21.63, -14.1) * mm, "end": v(-21.26, -13.64) * mm});
            skLineSegment(sketch, "E1060", {"start": v(-21.26, -13.64) * mm, "end": v(-21.1, -13.52) * mm});
            skLineSegment(sketch, "E1061", {"start": v(-21.1, -13.52) * mm, "end": v(-20.9, -13.4) * mm});
            skLineSegment(sketch, "E1062", {"start": v(-20.9, -13.4) * mm, "end": v(-20.18, -13.14) * mm});
            skLineSegment(sketch, "E1063", {"start": v(-20.18, -13.14) * mm, "end": v(-19.15, -13.05) * mm});
            skLineSegment(sketch, "E1064", {"start": v(-19.15, -13.05) * mm, "end": v(-18.05, -13.22) * mm});
            skLineSegment(sketch, "E1065", {"start": v(-18.05, -13.22) * mm, "end": v(-16.9, -13.64) * mm});
            skLineSegment(sketch, "E1066", {"start": v(-16.9, -13.64) * mm, "end": v(-15.74, -14.28) * mm});
            skLineSegment(sketch, "E1067", {"start": v(-15.74, -14.28) * mm, "end": v(-14.58, -15.1) * mm});
            skLineSegment(sketch, "E1068", {"start": v(-14.58, -15.1) * mm, "end": v(-13.45, -16.1) * mm});
            skLineSegment(sketch, "E1069", {"start": v(-13.45, -16.1) * mm, "end": v(-12.63, -16.95) * mm});
            skLineSegment(sketch, "E1070", {"start": v(-12.63, -16.95) * mm, "end": v(-12.37, -17.25) * mm});
            skLineSegment(sketch, "E1071", {"start": v(12.3, -16.32) * mm, "end": v(12.05, -16.62) * mm});
            skLineSegment(sketch, "E1072", {"start": v(12.05, -16.62) * mm, "end": v(11.38, -17.58) * mm});
            skLineSegment(sketch, "E1073", {"start": v(11.38, -17.58) * mm, "end": v(10.59, -19) * mm});
            skLineSegment(sketch, "E1074", {"start": v(10.59, -19) * mm, "end": v(9.96, -20.52) * mm});
            skLineSegment(sketch, "E1075", {"start": v(9.96, -20.52) * mm, "end": v(9.52, -22.04) * mm});
            skLineSegment(sketch, "E1076", {"start": v(9.52, -22.04) * mm, "end": v(9.29, -23.5) * mm});
            skLineSegment(sketch, "E1077", {"start": v(9.29, -23.5) * mm, "end": v(9.3, -24.84) * mm});
            skLineSegment(sketch, "E1078", {"start": v(9.3, -24.84) * mm, "end": v(9.57, -25.97) * mm});
            skLineSegment(sketch, "E1079", {"start": v(9.57, -25.97) * mm, "end": v(9.95, -26.64) * mm});
            skLineSegment(sketch, "E1080", {"start": v(9.95, -26.64) * mm, "end": v(10.13, -26.8) * mm});
            skLineSegment(sketch, "E1081", {"start": v(10.13, -26.8) * mm, "end": v(10.32, -26.95) * mm});
            skLineSegment(sketch, "E1082", {"start": v(10.32, -26.95) * mm, "end": v(10.96, -27.25) * mm});
            skLineSegment(sketch, "E1083", {"start": v(10.96, -27.25) * mm, "end": v(12.02, -27.5) * mm});
            skLineSegment(sketch, "E1084", {"start": v(12.02, -27.5) * mm, "end": v(13.26, -27.54) * mm});
            skLineSegment(sketch, "E1085", {"start": v(13.26, -27.54) * mm, "end": v(14.65, -27.3) * mm});
            skLineSegment(sketch, "E1086", {"start": v(14.65, -27.3) * mm, "end": v(16.11, -26.77) * mm});
            skLineSegment(sketch, "E1087", {"start": v(16.11, -26.77) * mm, "end": v(17.61, -25.9) * mm});
            skLineSegment(sketch, "E1088", {"start": v(17.61, -25.9) * mm, "end": v(19.1, -24.65) * mm});
            skLineSegment(sketch, "E1089", {"start": v(19.1, -24.65) * mm, "end": v(20.19, -23.42) * mm});
            skLineSegment(sketch, "E1090", {"start": v(20.19, -23.42) * mm, "end": v(20.5, -22.98) * mm});
            skLineSegment(sketch, "E1091", {"start": v(20.5, -22.98) * mm, "end": v(20.75, -22.67) * mm});
            skLineSegment(sketch, "E1092", {"start": v(20.75, -22.67) * mm, "end": v(21.33, -21.62) * mm});
            skLineSegment(sketch, "E1093", {"start": v(21.33, -21.62) * mm, "end": v(21.87, -20.12) * mm});
            skLineSegment(sketch, "E1094", {"start": v(21.87, -20.12) * mm, "end": v(22.14, -18.56) * mm});
            skLineSegment(sketch, "E1095", {"start": v(22.14, -18.56) * mm, "end": v(22.18, -17) * mm});
            skLineSegment(sketch, "E1096", {"start": v(22.18, -17) * mm, "end": v(22.03, -15.55) * mm});
            skLineSegment(sketch, "E1097", {"start": v(22.03, -15.55) * mm, "end": v(21.72, -14.25) * mm});
            skLineSegment(sketch, "E1098", {"start": v(21.72, -14.25) * mm, "end": v(21.28, -13.2) * mm});
            skLineSegment(sketch, "E1099", {"start": v(21.28, -13.2) * mm, "end": v(20.91, -12.6) * mm});
            skLineSegment(sketch, "E1100", {"start": v(20.91, -12.6) * mm, "end": v(20.75, -12.45) * mm});
            skLineSegment(sketch, "E1101", {"start": v(20.75, -12.45) * mm, "end": v(20.56, -12.3) * mm});
            skLineSegment(sketch, "E1102", {"start": v(20.56, -12.3) * mm, "end": v(19.87, -11.98) * mm});
            skLineSegment(sketch, "E1103", {"start": v(19.87, -11.98) * mm, "end": v(18.91, -11.85) * mm});
            skLineSegment(sketch, "E1104", {"start": v(18.91, -11.85) * mm, "end": v(17.89, -12.02) * mm});
            skLineSegment(sketch, "E1105", {"start": v(17.89, -12.02) * mm, "end": v(16.82, -12.47) * mm});
            skLineSegment(sketch, "E1106", {"start": v(16.82, -12.47) * mm, "end": v(15.7, -13.15) * mm});
            skLineSegment(sketch, "E1107", {"start": v(15.7, -13.15) * mm, "end": v(14.58, -14.05) * mm});
            skLineSegment(sketch, "E1108", {"start": v(14.58, -14.05) * mm, "end": v(13.44, -15.11) * mm});
            skLineSegment(sketch, "E1109", {"start": v(13.44, -15.11) * mm, "end": v(12.58, -16.01) * mm});
            skLineSegment(sketch, "E1110", {"start": v(12.58, -16.01) * mm, "end": v(12.3, -16.32) * mm});
            skLineSegment(sketch, "E1111", {"start": v(12.3, -16.32) * mm, "end": v(12.3, -16.32) * mm});
            skSolve(sketch);
        }
        {
            var Q0;
            Q0 = qSketchRegion(id + "F0", true);
            extrude(context, id + "F1", {"entities" : qUnion([Q0]), "depth" : 30 * mm, "offsetDistance" : 25 * mm});
        }
        {
            var Q0;
            Q0=makeQuery(id+"F0.imprint","IMPRINT",FACE,{"disambiguationData":[TD([[makeQuery(id+"F0.imprint","IMPRINT",EDGE,{"derivedFrom":sQuery(id+"F0.wireOp",EDGE,"E0.bottom")}),-1.0]])]});
            extrude(context, id + "F2", {"entities" : qUnion([Q0]), "operationType" : NewBodyOperationType.ADD, "depth" : 28 * mm, "offsetDistance" : 25 * mm});
        }
        {
            var Q0;
            Q0=makeQuery(id+"F0.imprint","IMPRINT",FACE,{"disambiguationData":[TD([[makeQuery(id+"F0.imprint","IMPRINT",EDGE,{"derivedFrom":sQuery(id+"F0.wireOp",EDGE,"E1.bottom")}),-1.0]])]});
            var Q1;
            Q1=makeQuery(id+"F0.imprint","IMPRINT",FACE,{"disambiguationData":[TD([[makeQuery(id+"F0.imprint","IMPRINT",EDGE,{"derivedFrom":sQuery(id+"F0.wireOp",EDGE,"E5")}),1.0]])]});
            extrude(context, id + "F3", {"entities" : qUnion([Q0, Q1]), "operationType" : NewBodyOperationType.ADD, "depth" : 2 * mm, "offsetDistance" : 25 * mm});
        }
        {
            var Q0;
            Q0=makeQuery(id+"F1.opExtrude","SWEPT_FACE",FACE,{"disambiguationData":[OSD([sQuery(id+"F0.wireOp",EDGE,"E2.bottom")])]});
            var sketch = newSketch(context, id + "F4", { "sketchPlane" : qUnion([Q0])});
            skLineSegment(sketch, "E1112.bottom", {"start": v(-26.5, 24) * mm, "end": v(26.5, 24) * mm});
            skLineSegment(sketch, "E1112.top", {"start": v(-26.5, 6) * mm, "end": v(26.5, 6) * mm});
            skLineSegment(sketch, "E1112.left", {"start": v(-26.5, 24) * mm, "end": v(-26.5, 6) * mm});
            skLineSegment(sketch, "E1112.right", {"start": v(26.5, 24) * mm, "end": v(26.5, 6) * mm});
            skPoint(sketch, "E1113", {"position": v(0, 6) * mm});
            skSolve(sketch);
        }
        {
            var Q0;
            Q0 = qSketchRegion(id + "F4", true);
            extrude(context, id + "F5", {"entities" : qUnion([Q0]), "operationType" : NewBodyOperationType.REMOVE, "endBound" : BoundingType.UP_TO_NEXT, "oppositeDirection" : true, "depth" : 25 * mm, "offsetDistance" : 25 * mm});
        }
        {
            var Q0;
            Q0=makeQuery(id+"F1.opExtrude","SWEPT_FACE",FACE,{"disambiguationData":[OSD([sQuery(id+"F0.wireOp",EDGE,"E2.right")])]});
            var sketch = newSketch(context, id + "F6", { "sketchPlane" : qUnion([Q0])});
            skLineSegment(sketch, "E1114.bottom", {"start": v(-37.5, 11) * mm, "end": v(-27.5, 11) * mm});
            skLineSegment(sketch, "E1114.top", {"start": v(-37.5, 5) * mm, "end": v(-27.5, 5) * mm});
            skLineSegment(sketch, "E1114.left", {"start": v(-37.5, 11) * mm, "end": v(-37.5, 5) * mm});
            skLineSegment(sketch, "E1114.right", {"start": v(-27.5, 11) * mm, "end": v(-27.5, 5) * mm});
            skLineSegment(sketch, "E1115.bottom", {"start": v(-19.5, 13) * mm, "end": v(-2.5, 13) * mm});
            skLineSegment(sketch, "E1115.top", {"start": v(-19.5, 6) * mm, "end": v(-2.5, 6) * mm});
            skLineSegment(sketch, "E1115.left", {"start": v(-19.5, 13) * mm, "end": v(-19.5, 6) * mm});
            skLineSegment(sketch, "E1115.right", {"start": v(-2.5, 13) * mm, "end": v(-2.5, 6) * mm});
            skCircle(sketch, "E1116", {"center": v(10.5, 9) * mm, "radius": 5 * mm});
            skSolve(sketch);
        }
        {
            var Q0;
            Q0 = qSketchRegion(id + "F6", true);
            extrude(context, id + "F7", {"entities" : qUnion([Q0]), "operationType" : NewBodyOperationType.REMOVE, "endBound" : BoundingType.UP_TO_NEXT, "oppositeDirection" : true, "depth" : 25 * mm, "offsetDistance" : 25 * mm});
        }
        {
            var Q0;
            Q0=makeQuery(id+"F1.opExtrude","SWEPT_FACE",FACE,{"disambiguationData":[OSD([sQuery(id+"F0.wireOp",EDGE,"E2.right")])]});
            var sketch = newSketch(context, id + "F8", { "sketchPlane" : qUnion([Q0])});
            skLineSegment(sketch, "E1117.bottom", {"start": v(-40.5, 17) * mm, "end": v(17.5, 17) * mm});
            skLineSegment(sketch, "E1117.top", {"start": v(-40.5, 2) * mm, "end": v(17.5, 2) * mm});
            skLineSegment(sketch, "E1117.left", {"start": v(-41.5, 16) * mm, "end": v(-41.5, 3) * mm});
            skLineSegment(sketch, "E1117.right", {"start": v(18.5, 16) * mm, "end": v(18.5, 3) * mm});
            skPoint(sketch, "E1118.visualSharp", {"position": v(-41.5, 17) * mm});
            skArc(sketch, "E1118.filletArc", {"start": v(-40.5, 17) * mm, "mid": v(-41.2, 16.7) * mm, "end": v(-41.5, 16) * mm});
            skPoint(sketch, "E1119.visualSharp", {"position": v(18.5, 17) * mm});
            skArc(sketch, "E1119.filletArc", {"start": v(18.5, 16) * mm, "mid": v(18.2, 16.7) * mm, "end": v(17.5, 17) * mm});
            skPoint(sketch, "E1120.visualSharp", {"position": v(18.5, 2) * mm});
            skArc(sketch, "E1120.filletArc", {"start": v(17.5, 2) * mm, "mid": v(18.2, 2.3) * mm, "end": v(18.5, 3) * mm});
            skPoint(sketch, "E1121.visualSharp", {"position": v(-41.5, 2) * mm});
            skArc(sketch, "E1121.filletArc", {"start": v(-41.5, 3) * mm, "mid": v(-41.2, 2.3) * mm, "end": v(-40.5, 2) * mm});
            skSolve(sketch);
        }
        {
            var Q0;
            Q0 = qSketchRegion(id + "F8", true);
            extrude(context, id + "F9", {"entities" : qUnion([Q0]), "operationType" : NewBodyOperationType.REMOVE, "oppositeDirection" : true, "depth" : 1 * mm, "offsetDistance" : 25 * mm});
        }
        {
            var Q0;
            Q0=makeQuery(id+"F9.boolean.opBoolean","COPY",EDGE,{"derivedFrom":makeQuery(id+"F9.opExtrude","CAP_EDGE",EDGE,{"disambiguationData":[OSD([sQuery(id+"F8.wireOp",EDGE,"E1117.bottom")])],"isStart":false})});
            var Q1;
            Q1=makeQuery(id+"F7.boolean.opBoolean","COPY",EDGE,{"derivedFrom":makeQuery(id+"F7.opExtrude","SWEPT_EDGE",EDGE,{"disambiguationData":[OSD([sQuery(id+"F6.wireOp",EDGE,"E1114.top"),sQuery(id+"F6.wireOp",EDGE,"E1114.right")])]})});
            var Q2;
            Q2=makeQuery(id+"F7.boolean.opBoolean","COPY",EDGE,{"derivedFrom":makeQuery(id+"F7.opExtrude","SWEPT_EDGE",EDGE,{"disambiguationData":[OSD([sQuery(id+"F6.wireOp",EDGE,"E1114.bottom"),sQuery(id+"F6.wireOp",EDGE,"E1114.right")])]})});
            var Q3;
            Q3=makeQuery(id+"F7.boolean.opBoolean","COPY",EDGE,{"derivedFrom":makeQuery(id+"F7.opExtrude","SWEPT_EDGE",EDGE,{"disambiguationData":[OSD([sQuery(id+"F6.wireOp",EDGE,"E1114.bottom"),sQuery(id+"F6.wireOp",EDGE,"E1114.left")])]})});
            var Q4;
            Q4=makeQuery(id+"F7.boolean.opBoolean","COPY",EDGE,{"derivedFrom":makeQuery(id+"F7.opExtrude","SWEPT_EDGE",EDGE,{"disambiguationData":[OSD([sQuery(id+"F6.wireOp",EDGE,"E1114.top"),sQuery(id+"F6.wireOp",EDGE,"E1114.left")])]})});
            var Q5;
            Q5=makeQuery(id+"F7.boolean.opBoolean","COPY",EDGE,{"derivedFrom":makeQuery(id+"F7.opExtrude","SWEPT_EDGE",EDGE,{"disambiguationData":[OSD([sQuery(id+"F6.wireOp",EDGE,"E1115.bottom"),sQuery(id+"F6.wireOp",EDGE,"E1115.left")])]})});
            var Q6;
            Q6=makeQuery(id+"F7.boolean.opBoolean","COPY",EDGE,{"derivedFrom":makeQuery(id+"F7.opExtrude","SWEPT_EDGE",EDGE,{"disambiguationData":[OSD([sQuery(id+"F6.wireOp",EDGE,"E1115.top"),sQuery(id+"F6.wireOp",EDGE,"E1115.left")])]})});
            var Q7;
            Q7=makeQuery(id+"F7.boolean.opBoolean","COPY",EDGE,{"derivedFrom":makeQuery(id+"F7.opExtrude","SWEPT_EDGE",EDGE,{"disambiguationData":[OSD([sQuery(id+"F6.wireOp",EDGE,"E1115.bottom"),sQuery(id+"F6.wireOp",EDGE,"E1115.right")])]})});
            var Q8;
            Q8=makeQuery(id+"F7.boolean.opBoolean","COPY",EDGE,{"derivedFrom":makeQuery(id+"F7.opExtrude","SWEPT_EDGE",EDGE,{"disambiguationData":[OSD([sQuery(id+"F6.wireOp",EDGE,"E1115.top"),sQuery(id+"F6.wireOp",EDGE,"E1115.right")])]})});
            var Q9;
            Q9=makeQuery(id+"F5.boolean.opBoolean","COPY",EDGE,{"derivedFrom":makeQuery(id+"F5.opExtrude","SWEPT_EDGE",EDGE,{"disambiguationData":[OSD([sQuery(id+"F4.wireOp",EDGE,"E1112.top"),sQuery(id+"F4.wireOp",EDGE,"E1112.left")])]})});
            var Q10;
            Q10=makeQuery(id+"F5.boolean.opBoolean","COPY",EDGE,{"derivedFrom":makeQuery(id+"F5.opExtrude","SWEPT_EDGE",EDGE,{"disambiguationData":[OSD([sQuery(id+"F4.wireOp",EDGE,"E1112.bottom"),sQuery(id+"F4.wireOp",EDGE,"E1112.left")])]})});
            var Q11;
            Q11=makeQuery(id+"F5.boolean.opBoolean","COPY",EDGE,{"derivedFrom":makeQuery(id+"F5.opExtrude","SWEPT_EDGE",EDGE,{"disambiguationData":[OSD([sQuery(id+"F4.wireOp",EDGE,"E1112.bottom"),sQuery(id+"F4.wireOp",EDGE,"E1112.right")])]})});
            var Q12;
            Q12=makeQuery(id+"F5.boolean.opBoolean","COPY",EDGE,{"derivedFrom":makeQuery(id+"F5.opExtrude","SWEPT_EDGE",EDGE,{"disambiguationData":[OSD([sQuery(id+"F4.wireOp",EDGE,"E1112.top"),sQuery(id+"F4.wireOp",EDGE,"E1112.right")])]})});
            var Q13;
            Q13=makeQuery(id+"F1.opExtrude","SWEPT_EDGE",EDGE,{"disambiguationData":[OSD([sQuery(id+"F0.wireOp",EDGE,"E2.top"),sQuery(id+"F0.wireOp",EDGE,"E2.right")])]});
            var Q14;
            Q14=makeQuery(id+"F1.opExtrude","CAP_EDGE",EDGE,{"disambiguationData":[OSD([sQuery(id+"F0.wireOp",EDGE,"E2.right")])],"isStart":true});
            var Q15;
            Q15=makeQuery(id+"F1.opExtrude","CAP_EDGE",EDGE,{"disambiguationData":[OSD([sQuery(id+"F0.wireOp",EDGE,"E2.top")])],"isStart":true});
            var Q16;
            Q16=makeQuery(id+"F1.opExtrude","CAP_EDGE",EDGE,{"disambiguationData":[OSD([sQuery(id+"F0.wireOp",EDGE,"E2.left")])],"isStart":true});
            var Q17;
            Q17=makeQuery(id+"F1.opExtrude","CAP_EDGE",EDGE,{"disambiguationData":[OSD([sQuery(id+"F0.wireOp",EDGE,"E2.bottom")])],"isStart":true});
            var Q18;
            Q18=makeQuery(id+"F1.opExtrude","SWEPT_EDGE",EDGE,{"disambiguationData":[OSD([sQuery(id+"F0.wireOp",EDGE,"E2.top"),sQuery(id+"F0.wireOp",EDGE,"E2.left")])]});
            var Q19;
            Q19=makeQuery(id+"F1.opExtrude","SWEPT_EDGE",EDGE,{"disambiguationData":[OSD([sQuery(id+"F0.wireOp",EDGE,"E2.bottom"),sQuery(id+"F0.wireOp",EDGE,"E2.left")])]});
            var Q20;
            Q20=makeQuery(id+"F1.opExtrude","SWEPT_EDGE",EDGE,{"disambiguationData":[OSD([sQuery(id+"F0.wireOp",EDGE,"E2.bottom"),sQuery(id+"F0.wireOp",EDGE,"E2.right")])]});
            fillet(context, id + "F10", {"entities" : qUnion([Q0, Q1, Q2, Q3, Q4, Q5, Q6, Q7, Q8, Q9, Q10, Q11, Q12, Q13, Q14, Q15, Q16, Q17, Q18, Q19, Q20]), "radius" : 2 * mm, "tangentPropagation" : true, "allowEdgeOverflow" : false});
        }
        {
            var Q0;
            Q0=makeQuery(id+"F7.boolean.opBoolean","COPY",FACE,{"derivedFrom":makeQuery(id+"F7.opExtrude","SWEPT_FACE",FACE,{"disambiguationData":[OSD([sQuery(id+"F6.wireOp",EDGE,"E1115.top")])]})});
            var Q1;
            Q1=makeQuery(id+"F7.boolean.opBoolean","COPY",FACE,{"derivedFrom":makeQuery(id+"F7.opExtrude","SWEPT_FACE",FACE,{"disambiguationData":[OSD([sQuery(id+"F6.wireOp",EDGE,"E1116")])]})});
            var Q2;
            Q2=makeQuery(id+"F7.boolean.opBoolean","COPY",FACE,{"derivedFrom":makeQuery(id+"F7.opExtrude","SWEPT_FACE",FACE,{"disambiguationData":[OSD([sQuery(id+"F6.wireOp",EDGE,"E1114.top")])]})});
            fillet(context, id + "F11", {"entities" : qUnion([Q0, Q1, Q2]), "radius" : .5 * mm, "tangentPropagation" : true, "allowEdgeOverflow" : false});
        }
        {
            var Q0;
            Q0=makeQuery(id+"F5.boolean.opBoolean","COPY",FACE,{"derivedFrom":makeQuery(id+"F5.opExtrude","SWEPT_FACE",FACE,{"disambiguationData":[OSD([sQuery(id+"F4.wireOp",EDGE,"E1112.top")])]})});
            fillet(context, id + "F12", {"entities" : qUnion([Q0]), "radius" : 1 * mm, "tangentPropagation" : true, "allowEdgeOverflow" : false});
        }
    });
